FCSTD DOCUMENT  (FreeCAD 0.18R16146 (Git))
Label: body_polywood_8mm
License: All rights reserved
LicenseURL: http://en.wikipedia.org/wiki/All_rights_reserved
objects: Sketcher::SketchObject×6
note: 6 computed .brp shape members not serialized (recipe doc carries the construction recipe); baked Part::Feature solids carry a one-line shape summary decoded from their .brp

FEATURE [Sketcher::SketchObject] Sketch  label="bottom"
  sketch-geometry (118):
    g0: LineSegment [constr] StartX=-110 StartY=110 StartZ=0 EndX=110 EndY=110 EndZ=0
    g1: LineSegment [constr] StartX=110 StartY=110 StartZ=0 EndX=110 EndY=-110 EndZ=0
    g2: LineSegment [constr] StartX=110 StartY=-110 StartZ=0 EndX=-110 EndY=-110 EndZ=0
    g3: LineSegment [constr] StartX=-110 StartY=-110 StartZ=0 EndX=-110 EndY=110 EndZ=0
    g4: Circle CenterX=-104.5 CenterY=104.5 CenterZ=0 NormalX=0 NormalY=0 NormalZ=1 AngleXU=0 Radius=1.55
    g5: Circle CenterX=104.5 CenterY=104.5 CenterZ=0 NormalX=0 NormalY=0 NormalZ=1 AngleXU=0 Radius=1.55
    g6: Circle CenterX=-104.5 CenterY=-104.5 CenterZ=0 NormalX=0 NormalY=0 NormalZ=1 AngleXU=0 Radius=1.55
    g7: Circle CenterX=104.5 CenterY=-104.5 CenterZ=0 NormalX=0 NormalY=0 NormalZ=1 AngleXU=0 Radius=1.55
    g8: LineSegment [constr] StartX=-104.5 StartY=104.5 StartZ=0 EndX=104.5 EndY=104.5 EndZ=0
    g9: LineSegment [constr] StartX=104.5 StartY=104.5 StartZ=0 EndX=104.5 EndY=-104.5 EndZ=0
    g10: LineSegment [constr] StartX=104.5 StartY=-104.5 StartZ=0 EndX=-104.5 EndY=-104.5 EndZ=0
    g11: LineSegment [constr] StartX=-104.5 StartY=-104.5 StartZ=0 EndX=-104.5 EndY=104.5 EndZ=0
    g12: LineSegment [constr] StartX=0 StartY=0 StartZ=0 EndX=0 EndY=210 EndZ=0
    g13: LineSegment [constr] StartX=0 StartY=0 StartZ=0 EndX=181.865 EndY=-105 EndZ=0
    g14: LineSegment [constr] StartX=0 StartY=0 StartZ=0 EndX=-181.865 EndY=-105 EndZ=0
    g15: LineSegment [constr] StartX=-33 StartY=202.5 StartZ=0 EndX=33 EndY=202.5 EndZ=0
    g16: Circle CenterX=-33 CenterY=202.5 CenterZ=0 NormalX=0 NormalY=0 NormalZ=1 AngleXU=0 Radius=2.1
    g17: Circle CenterX=33 CenterY=202.5 CenterZ=0 NormalX=0 NormalY=0 NormalZ=1 AngleXU=0 Radius=2.1
    g18: LineSegment [constr] StartX=158.87 StartY=-129.829 StartZ=0 EndX=191.87 EndY=-72.6712 EndZ=0
    g19: LineSegment [constr] StartX=-158.87 StartY=-129.829 StartZ=0 EndX=-191.87 EndY=-72.6712 EndZ=0
    g20: GeomPoint X=-175.37 Y=-101.25 Z=0
    g21: GeomPoint X=175.37 Y=-101.25 Z=0
    g22: Circle CenterX=-158.87 CenterY=-129.829 CenterZ=0 NormalX=0 NormalY=0 NormalZ=1 AngleXU=0 Radius=2.1
    g23: Circle CenterX=-191.87 CenterY=-72.6712 CenterZ=0 NormalX=0 NormalY=0 NormalZ=1 AngleXU=0 Radius=2.1
    g24: Circle CenterX=158.87 CenterY=-129.829 CenterZ=0 NormalX=0 NormalY=0 NormalZ=1 AngleXU=0 Radius=2.1
    g25: Circle CenterX=191.87 CenterY=-72.6712 CenterZ=0 NormalX=0 NormalY=0 NormalZ=1 AngleXU=0 Radius=2.1
    g26: LineSegment [constr] StartX=-202.5 StartY=-139.829 StartZ=0 EndX=202.5 EndY=-139.829 EndZ=0
    g27: LineSegment [constr] StartX=202.5 StartY=-139.829 StartZ=0 EndX=202.5 EndY=210 EndZ=0
    g28: LineSegment [constr] StartX=202.5 StartY=210 StartZ=0 EndX=-202.5 EndY=210 EndZ=0
    g29: LineSegment [constr] StartX=-202.5 StartY=210 StartZ=0 EndX=-202.5 EndY=-139.829 EndZ=0
    g30: LineSegment [constr] StartX=-145.5 StartY=-139.829 StartZ=0 EndX=-115.5 EndY=-139.829 EndZ=0
    g31: LineSegment StartX=-115.5 StartY=-139.829 StartZ=0 EndX=-115.5 EndY=-147.829 EndZ=0
    g32: LineSegment StartX=-115.5 StartY=-147.829 StartZ=0 EndX=-145.5 EndY=-147.829 EndZ=0
    g33: LineSegment StartX=-145.5 StartY=-147.829 StartZ=0 EndX=-145.5 EndY=-139.829 EndZ=0
    g34: LineSegment [constr] StartX=-58.5 StartY=-139.829 StartZ=0 EndX=-28.5 EndY=-139.829 EndZ=0
    g35: LineSegment StartX=-28.5 StartY=-139.829 StartZ=0 EndX=-28.5 EndY=-147.829 EndZ=0
    g36: LineSegment StartX=-28.5 StartY=-147.829 StartZ=0 EndX=-58.5 EndY=-147.829 EndZ=0
    g37: LineSegment StartX=-58.5 StartY=-147.829 StartZ=0 EndX=-58.5 EndY=-139.829 EndZ=0
    g38: LineSegment [constr] StartX=28.5 StartY=-139.829 StartZ=0 EndX=58.5 EndY=-139.829 EndZ=0
    g39: LineSegment StartX=58.5 StartY=-139.829 StartZ=0 EndX=58.5 EndY=-147.829 EndZ=0
    g40: LineSegment StartX=58.5 StartY=-147.829 StartZ=0 EndX=28.5 EndY=-147.829 EndZ=0
    g41: LineSegment StartX=28.5 StartY=-147.829 StartZ=0 EndX=28.5 EndY=-139.829 EndZ=0
    g42: LineSegment [constr] StartX=115.5 StartY=-139.829 StartZ=0 EndX=145.5 EndY=-139.829 EndZ=0
    g43: LineSegment StartX=145.5 StartY=-139.829 StartZ=0 EndX=145.5 EndY=-147.829 EndZ=0
    g44: LineSegment StartX=145.5 StartY=-147.829 StartZ=0 EndX=115.5 EndY=-147.829 EndZ=0
    g45: LineSegment StartX=115.5 StartY=-147.829 StartZ=0 EndX=115.5 EndY=-139.829 EndZ=0
    g46: LineSegment StartX=202.5 StartY=-63.8631 StartZ=0 EndX=210.5 EndY=-63.8631 EndZ=0
    g47: LineSegment StartX=210.5 StartY=-63.8631 StartZ=0 EndX=210.5 EndY=-93.8631 EndZ=0
    g48: LineSegment StartX=210.5 StartY=-93.8631 StartZ=0 EndX=202.5 EndY=-93.8631 EndZ=0
    g49: LineSegment [constr] StartX=202.5 StartY=-93.8631 StartZ=0 EndX=202.5 EndY=-63.8631 EndZ=0
    g50: LineSegment StartX=202.5 StartY=12.1027 StartZ=0 EndX=210.5 EndY=12.1027 EndZ=0
    g51: LineSegment StartX=210.5 StartY=12.1027 StartZ=0 EndX=210.5 EndY=-17.8973 EndZ=0
    g52: LineSegment StartX=210.5 StartY=-17.8973 StartZ=0 EndX=202.5 EndY=-17.8973 EndZ=0
    g53: LineSegment [constr] StartX=202.5 StartY=-17.8973 StartZ=0 EndX=202.5 EndY=12.1027 EndZ=0
    g54: LineSegment StartX=202.5 StartY=88.0685 StartZ=0 EndX=210.5 EndY=88.0685 EndZ=0
    g55: LineSegment StartX=210.5 StartY=88.0685 StartZ=0 EndX=210.5 EndY=58.0685 EndZ=0
    g56: LineSegment StartX=210.5 StartY=58.0685 StartZ=0 EndX=202.5 EndY=58.0685 EndZ=0
    g57: LineSegment [constr] StartX=202.5 StartY=58.0685 StartZ=0 EndX=202.5 EndY=88.0685 EndZ=0
    g58: LineSegment StartX=202.5 StartY=164.034 StartZ=0 EndX=210.5 EndY=164.034 EndZ=0
    g59: LineSegment StartX=210.5 StartY=164.034 StartZ=0 EndX=210.5 EndY=134.034 EndZ=0
    g60: LineSegment StartX=210.5 StartY=134.034 StartZ=0 EndX=202.5 EndY=134.034 EndZ=0
    g61: LineSegment [constr] StartX=202.5 StartY=134.034 StartZ=0 EndX=202.5 EndY=164.034 EndZ=0
    g62: LineSegment StartX=-145.5 StartY=218 StartZ=0 EndX=-115.5 EndY=218 EndZ=0
    g63: LineSegment StartX=-115.5 StartY=218 StartZ=0 EndX=-115.5 EndY=210 EndZ=0
    g64: LineSegment [constr] StartX=-115.5 StartY=210 StartZ=0 EndX=-145.5 EndY=210 EndZ=0
    g65: LineSegment StartX=-145.5 StartY=210 StartZ=0 EndX=-145.5 EndY=218 EndZ=0
    g66: LineSegment StartX=-58.5 StartY=218 StartZ=0 EndX=-28.5 EndY=218 EndZ=0
    g67: LineSegment StartX=-28.5 StartY=218 StartZ=0 EndX=-28.5 EndY=210 EndZ=0
    g68: LineSegment [constr] StartX=-28.5 StartY=210 StartZ=0 EndX=-58.5 EndY=210 EndZ=0
    g69: LineSegment StartX=-58.5 StartY=210 StartZ=0 EndX=-58.5 EndY=218 EndZ=0
    g70: LineSegment StartX=28.5 StartY=218 StartZ=0 EndX=58.5 EndY=218 EndZ=0
    g71: LineSegment StartX=58.5 StartY=218 StartZ=0 EndX=58.5 EndY=210 EndZ=0
    g72: LineSegment [constr] StartX=58.5 StartY=210 StartZ=0 EndX=28.5 EndY=210 EndZ=0
    g73: LineSegment StartX=28.5 StartY=210 StartZ=0 EndX=28.5 EndY=218 EndZ=0
    g74: LineSegment StartX=115.5 StartY=218 StartZ=0 EndX=145.5 EndY=218 EndZ=0
    g75: LineSegment StartX=145.5 StartY=218 StartZ=0 EndX=145.5 EndY=210 EndZ=0
    g76: LineSegment [constr] StartX=145.5 StartY=210 StartZ=0 EndX=115.5 EndY=210 EndZ=0
    g77: LineSegment StartX=115.5 StartY=210 StartZ=0 EndX=115.5 EndY=218 EndZ=0
    g78: LineSegment StartX=-210.5 StartY=164.034 StartZ=0 EndX=-202.5 EndY=164.034 EndZ=0
    g79: LineSegment [constr] StartX=-202.5 StartY=164.034 StartZ=0 EndX=-202.5 EndY=134.034 EndZ=0
    g80: LineSegment StartX=-202.5 StartY=134.034 StartZ=0 EndX=-210.5 EndY=134.034 EndZ=0
    g81: LineSegment StartX=-210.5 StartY=134.034 StartZ=0 EndX=-210.5 EndY=164.034 EndZ=0
    g82: LineSegment StartX=-210.5 StartY=88.0685 StartZ=0 EndX=-202.5 EndY=88.0685 EndZ=0
    g83: LineSegment [constr] StartX=-202.5 StartY=88.0685 StartZ=0 EndX=-202.5 EndY=58.0685 EndZ=0
    g84: LineSegment StartX=-202.5 StartY=58.0685 StartZ=0 EndX=-210.5 EndY=58.0685 EndZ=0
    g85: LineSegment StartX=-210.5 StartY=58.0685 StartZ=0 EndX=-210.5 EndY=88.0685 EndZ=0
    g86: LineSegment StartX=-210.5 StartY=12.1027 StartZ=0 EndX=-202.5 EndY=12.1027 EndZ=0
    g87: LineSegment [constr] StartX=-202.5 StartY=12.1027 StartZ=0 EndX=-202.5 EndY=-17.8973 EndZ=0
    g88: LineSegment StartX=-202.5 StartY=-17.8973 StartZ=0 EndX=-210.5 EndY=-17.8973 EndZ=0
    g89: LineSegment StartX=-210.5 StartY=-17.8973 StartZ=0 EndX=-210.5 EndY=12.1027 EndZ=0
    g90: LineSegment StartX=-210.5 StartY=-63.8631 StartZ=0 EndX=-202.5 EndY=-63.8631 EndZ=0
    g91: LineSegment [constr] StartX=-202.5 StartY=-63.8631 StartZ=0 EndX=-202.5 EndY=-93.8631 EndZ=0
    g92: LineSegment StartX=-202.5 StartY=-93.8631 StartZ=0 EndX=-210.5 EndY=-93.8631 EndZ=0
    g93: LineSegment StartX=-210.5 StartY=-93.8631 StartZ=0 EndX=-210.5 EndY=-63.8631 EndZ=0
    g94: LineSegment StartX=-28.5 StartY=-139.829 StartZ=0 EndX=28.5 EndY=-139.829 EndZ=0
    g95: LineSegment StartX=58.5 StartY=-139.829 StartZ=0 EndX=115.5 EndY=-139.829 EndZ=0
    g96: LineSegment StartX=145.5 StartY=-139.829 StartZ=0 EndX=202.5 EndY=-139.829 EndZ=0
    g97: LineSegment StartX=202.5 StartY=-139.829 StartZ=0 EndX=202.5 EndY=-93.8631 EndZ=0
    g98: LineSegment StartX=202.5 StartY=-63.8631 StartZ=0 EndX=202.5 EndY=-17.8973 EndZ=0
    g99: LineSegment StartX=202.5 StartY=12.1027 StartZ=0 EndX=202.5 EndY=58.0685 EndZ=0
    g100: LineSegment StartX=202.5 StartY=88.0685 StartZ=0 EndX=202.5 EndY=134.034 EndZ=0
    g101: LineSegment StartX=202.5 StartY=164.034 StartZ=0 EndX=202.5 EndY=210 EndZ=0
    g102: LineSegment StartX=145.5 StartY=210 StartZ=0 EndX=202.5 EndY=210 EndZ=0
    g103: LineSegment StartX=58.5 StartY=210 StartZ=0 EndX=115.5 EndY=210 EndZ=0
    g104: LineSegment StartX=-28.5 StartY=210 StartZ=0 EndX=28.5 EndY=210 EndZ=0
    g105: LineSegment StartX=-115.5 StartY=210 StartZ=0 EndX=-58.5 EndY=210 EndZ=0
    g106: LineSegment StartX=-202.5 StartY=210 StartZ=0 EndX=-145.5 EndY=210 EndZ=0
    g107: LineSegment StartX=-202.5 StartY=164.034 StartZ=0 EndX=-202.5 EndY=210 EndZ=0
    g108: LineSegment StartX=-202.5 StartY=88.0685 StartZ=0 EndX=-202.5 EndY=134.034 EndZ=0
    g109: LineSegment StartX=-202.5 StartY=12.1027 StartZ=0 EndX=-202.5 EndY=58.0685 EndZ=0
    g110: LineSegment StartX=-202.5 StartY=-63.8631 StartZ=0 EndX=-202.5 EndY=-17.8973 EndZ=0
    g111: LineSegment StartX=-202.5 StartY=-139.829 StartZ=0 EndX=-202.5 EndY=-93.8631 EndZ=0
    g112: LineSegment StartX=-202.5 StartY=-139.829 StartZ=0 EndX=-145.5 EndY=-139.829 EndZ=0
    g113: LineSegment StartX=-115.5 StartY=-139.829 StartZ=0 EndX=-58.5 EndY=-139.829 EndZ=0
    g114: Circle CenterX=-193.5 CenterY=201 CenterZ=0 NormalX=0 NormalY=0 NormalZ=1 AngleXU=0 Radius=1.55
    g115: Circle CenterX=193.5 CenterY=201 CenterZ=0 NormalX=0 NormalY=0 NormalZ=1 AngleXU=0 Radius=1.55
    g116: Circle CenterX=193.5 CenterY=-130.829 CenterZ=0 NormalX=0 NormalY=0 NormalZ=1 AngleXU=0 Radius=1.55
    g117: Circle CenterX=-193.5 CenterY=-130.829 CenterZ=0 NormalX=0 NormalY=0 NormalZ=1 AngleXU=0 Radius=1.55
  constraints (319):
    c: Coincident(g0,g1)
    c: Coincident(g1,g2)
    c: Coincident(g2,g3)
    c: Coincident(g3,g0)
    c: Horizontal(g0)
    c: Vertical(g3)
    c: Symmetric(g2,g1,g-2)
    c: Symmetric(g0,g1,g-1)
    c: DistanceX(g0,g0) = 220
    c: DistanceY(g1,g1) = 220
    c: Coincident(g8,g9)
    c: Coincident(g9,g10)
    c: Coincident(g10,g11)
    c: Coincident(g11,g8)
    c: Horizontal(g8)
    c: Horizontal(g10)
    c: Vertical(g9)
    c: Vertical(g11)
    c: Coincident(g7,g9)
    c: Coincident(g6,g10)
    c: Coincident(g4,g8)
    c: Coincident(g5,g8)
    c: DistanceY(g4,g0) = 5.5
    c: DistanceX(g0,g4) = 5.5
    c: DistanceX(g5,g0) = 5.5
    c: DistanceY(g2,g6) = 5.5
    c: Radius(g6) = 1.55
    c: Equal(g6,g7)
    c: Equal(g6,g4)
    c: Equal(g6,g5)
    c: Coincident(g12,g13)
    c: Coincident(g12,g14)
    c: Coincident(g12,g-1)
    c: Vertical(g12)
    c: Angle(g13,g12) = 2.0944
    c: Angle(g12,g14) = 2.0944
    c: Equal(g14,g12)
    c: Equal(g12,g13)
    c: DistanceY(g12,g12) = 210
    c: DistanceX(g15,g15) = 66
    c: Symmetric(g15,g15,g12)
    c: DistanceY(g15,g12) = 7.5
    c: Coincident(g15,g17)
    c: Coincident(g15,g16)
    c: Radius(g16) = 2.1
    c: Equal(g16,g17)
    c: Symmetric(g19,g19,g14)
    c: Symmetric(g18,g18,g13)
    c: Distance(g18) = 66
    c: Distance(g19) = 66
    c: PointOnObject(g20,g14)
    c: PointOnObject(g20,g19)
    c: Distance(g14,g20) = 7.5
    c: PointOnObject(g21,g13)
    c: PointOnObject(g21,g18)
    c: Distance(g21,g13) = 7.5
    c: Coincident(g18,g25)
    c: Coincident(g18,g24)
    c: Coincident(g19,g22)
    c: Coincident(g19,g23)
    c: Equal(g23,g22)
    c: Equal(g22,g24)
    c: Equal(g24,g25)
    c: Equal(g25,g17)
    c: Coincident(g26,g27)
    c: Coincident(g27,g28)
    c: Coincident(g28,g29)
    c: Coincident(g29,g26)
    c: Horizontal(g28)
    c: Vertical(g27)
    c: Vertical(g29)
    c: DistanceY(g16,g28) = 7.5
    c: DistanceY(g26,g24) = 10
    c: Coincident(g30,g31)
    c: Coincident(g31,g32)
    c: Coincident(g32,g33)
    c: Coincident(g33,g30)
    c: Horizontal(g30)
    c: Horizontal(g32)
    c: Vertical(g31)
    c: Vertical(g33)
    c: Coincident(g34,g35)
    c: Coincident(g35,g36)
    c: Coincident(g36,g37)
    c: Coincident(g37,g34)
    c: Horizontal(g34)
    c: Horizontal(g36)
    c: Vertical(g35)
    c: Vertical(g37)
    c: Coincident(g38,g39)
    c: Coincident(g39,g40)
    c: Coincident(g40,g41)
    c: Coincident(g41,g38)
    c: Horizontal(g38)
    c: Horizontal(g40)
    c: Vertical(g39)
    c: Vertical(g41)
    c: Coincident(g42,g43)
    c: Coincident(g43,g44)
    c: Coincident(g44,g45)
    c: Coincident(g45,g42)
    c: Horizontal(g42)
    c: Horizontal(g44)
    c: Vertical(g43)
    c: Vertical(g45)
    c: Coincident(g46,g47)
    c: Coincident(g47,g48)
    c: Coincident(g48,g49)
    c: Coincident(g49,g46)
    c: Horizontal(g46)
    c: Horizontal(g48)
    c: Vertical(g47)
    c: Vertical(g49)
    c: Coincident(g50,g51)
    c: Coincident(g51,g52)
    c: Coincident(g52,g53)
    c: Coincident(g53,g50)
    c: Horizontal(g50)
    c: Horizontal(g52)
    c: Vertical(g51)
    c: Vertical(g53)
    c: Coincident(g54,g55)
    c: Coincident(g55,g56)
    c: Coincident(g56,g57)
    c: Coincident(g57,g54)
    c: Horizontal(g54)
    c: Horizontal(g56)
    c: Vertical(g55)
    c: Vertical(g57)
    c: Coincident(g58,g59)
    c: Coincident(g59,g60)
    c: Coincident(g60,g61)
    c: Coincident(g61,g58)
    c: Horizontal(g58)
    c: Horizontal(g60)
    c: Vertical(g59)
    c: Vertical(g61)
    c: Coincident(g62,g63)
    c: Coincident(g63,g64)
    c: Coincident(g64,g65)
    c: Coincident(g65,g62)
    c: Horizontal(g62)
    c: Horizontal(g64)
    c: Vertical(g63)
    c: Vertical(g65)
    c: Coincident(g66,g67)
    c: Coincident(g67,g68)
    c: Coincident(g68,g69)
    c: Coincident(g69,g66)
    c: Horizontal(g66)
    c: Horizontal(g68)
    c: Vertical(g67)
    c: Vertical(g69)
    c: Coincident(g70,g71)
    c: Coincident(g71,g72)
    c: Coincident(g72,g73)
    c: Coincident(g73,g70)
    c: Horizontal(g70)
    c: Horizontal(g72)
    c: Vertical(g71)
    c: Vertical(g73)
    c: Coincident(g74,g75)
    c: Coincident(g75,g76)
    c: Coincident(g76,g77)
    c: Coincident(g77,g74)
    c: Horizontal(g74)
    c: Horizontal(g76)
    c: Vertical(g75)
    c: Vertical(g77)
    c: Coincident(g78,g79)
    c: Coincident(g79,g80)
    c: Coincident(g80,g81)
    c: Coincident(g81,g78)
    c: Horizontal(g78)
    c: Horizontal(g80)
    c: Vertical(g79)
    c: Vertical(g81)
    c: Coincident(g82,g83)
    c: Coincident(g83,g84)
    c: Coincident(g84,g85)
    c: Coincident(g85,g82)
    c: Horizontal(g82)
    c: Horizontal(g84)
    c: Vertical(g83)
    c: Vertical(g85)
    c: Coincident(g86,g87)
    c: Coincident(g87,g88)
    c: Coincident(g88,g89)
    c: Coincident(g89,g86)
    c: Horizontal(g86)
    c: Horizontal(g88)
    c: Vertical(g87)
    c: Vertical(g89)
    c: Coincident(g90,g91)
    c: Coincident(g91,g92)
    c: Coincident(g92,g93)
    c: Coincident(g93,g90)
    c: Horizontal(g90)
    c: Horizontal(g92)
    c: Vertical(g91)
    c: Vertical(g93)
    c: PointOnObject(g34,g26)
    c: PointOnObject(g30,g26)
    c: PointOnObject(g91,g29)
    c: PointOnObject(g87,g29)
    c: PointOnObject(g83,g29)
    c: PointOnObject(g79,g29)
    c: PointOnObject(g64,g28)
    c: PointOnObject(g68,g28)
    c: PointOnObject(g72,g28)
    c: PointOnObject(g76,g28)
    c: PointOnObject(g60,g27)
    c: PointOnObject(g56,g27)
    c: PointOnObject(g52,g27)
    c: PointOnObject(g48,g27)
    c: PointOnObject(g42,g26)
    c: PointOnObject(g38,g26)
    c: Equal(g39,g45)
    c: Equal(g45,g48)
    c: Equal(g48,g52)
    c: Equal(g52,g56)
    c: Equal(g56,g60)
    c: Equal(g60,g75)
    c: Equal(g75,g71)
    c: Equal(g71,g67)
    c: Equal(g67,g63)
    c: Equal(g63,g78)
    c: Equal(g78,g82)
    c: Equal(g82,g86)
    c: Equal(g86,g90)
    c: Equal(g90,g33)
    c: Equal(g33,g37)
    c: DistanceY(g65,g65) = 8
    c: Equal(g32,g36)
    c: Equal(g36,g40)
    c: Equal(g40,g44)
    c: Equal(g44,g47)
    c: Equal(g47,g51)
    c: Equal(g51,g55)
    c: Equal(g55,g59)
    c: Equal(g59,g74)
    c: Equal(g74,g70)
    c: Equal(g70,g66)
    c: Equal(g66,g62)
    c: Equal(g62,g81)
    c: Equal(g81,g85)
    c: Equal(g85,g89)
    c: Equal(g89,g93)
    c: DistanceX(g62,g62) = 30
    c: Coincident(g113,g30)
    c: Coincident(g113,g34)
    c: Coincident(g34,g94)
    c: Coincident(g38,g94)
    c: Coincident(g38,g95)
    c: Coincident(g42,g95)
    c: Coincident(g96,g42)
    c: Coincident(g26,g96)
    c: Coincident(g26,g97)
    c: Coincident(g48,g97)
    c: Coincident(g46,g98)
    c: Coincident(g52,g98)
    c: Coincident(g50,g99)
    c: Coincident(g56,g99)
    c: Coincident(g54,g100)
    c: Coincident(g60,g100)
    c: Coincident(g58,g101)
    c: Coincident(g27,g101)
    c: Coincident(g27,g102)
    c: Coincident(g75,g102)
    c: Coincident(g76,g103)
    c: Coincident(g71,g103)
    c: Coincident(g72,g104)
    c: Coincident(g67,g104)
    c: Coincident(g68,g105)
    c: Coincident(g63,g105)
    c: Coincident(g64,g106)
    c: Coincident(g28,g106)
    c: Coincident(g28,g107)
    c: Coincident(g78,g107)
    c: Coincident(g82,g108)
    c: Coincident(g79,g108)
    c: Coincident(g86,g109)
    c: Coincident(g83,g109)
    c: Coincident(g90,g110)
    c: Coincident(g87,g110)
    c: Coincident(g91,g111)
    c: Coincident(g26,g111)
    c: Coincident(g26,g112)
    c: Coincident(g30,g112)
    c: Equal(g97,g98)
    c: Equal(g98,g99)
    c: Equal(g99,g100)
    c: Equal(g100,g101)
    c: Equal(g106,g105)
    c: Equal(g105,g104)
    c: Equal(g104,g103)
    c: Equal(g103,g102)
    c: Equal(g107,g108)
    c: Equal(g108,g109)
    c: Equal(g109,g110)
    c: Equal(g110,g111)
    c: Equal(g112,g113)
    c: Equal(g113,g94)
    c: Equal(g94,g95)
    c: Equal(g95,g96)
    c: Symmetric(g111,g96,g-2)
    c: DistanceX(g111,g96) = 405
    c: DistanceX(g106,g114) = 9
    c: DistanceY(g114,g106) = 9
    c: Radius(g114) = 1.55
    c: DistanceX(g115,g101) = 9
    c: DistanceY(g115,g101) = 9
    c: Radius(g115) = 1.55
    c: DistanceX(g116,g96) = 9
    c: DistanceY(g96,g116) = 9
    c: Radius(g116) = 1.55
    c: DistanceX(g111,g117) = 9
    c: DistanceY(g111,g117) = 9
    c: Radius(g117) = 1.55
FEATURE [Sketcher::SketchObject] Sketch001  label="top"
  sketch-geometry (153):
    g0: LineSegment [constr] StartX=-110 StartY=110 StartZ=0 EndX=110 EndY=110 EndZ=0
    g1: LineSegment [constr] StartX=110 StartY=110 StartZ=0 EndX=110 EndY=-110 EndZ=0
    g2: LineSegment [constr] StartX=110 StartY=-110 StartZ=0 EndX=-110 EndY=-110 EndZ=0
    g3: LineSegment [constr] StartX=-110 StartY=-110 StartZ=0 EndX=-110 EndY=110 EndZ=0
    g4: Circle [constr] CenterX=-104.5 CenterY=104.5 CenterZ=0 NormalX=0 NormalY=0 NormalZ=1 AngleXU=0 Radius=1.55
    g5: Circle [constr] CenterX=104.5 CenterY=104.5 CenterZ=0 NormalX=0 NormalY=0 NormalZ=1 AngleXU=0 Radius=1.55
    g6: Circle [constr] CenterX=-104.5 CenterY=-104.5 CenterZ=0 NormalX=0 NormalY=0 NormalZ=1 AngleXU=0 Radius=1.55
    g7: Circle [constr] CenterX=104.5 CenterY=-104.5 CenterZ=0 NormalX=0 NormalY=0 NormalZ=1 AngleXU=0 Radius=1.55
    g8: LineSegment [constr] StartX=-104.5 StartY=104.5 StartZ=0 EndX=104.5 EndY=104.5 EndZ=0
    g9: LineSegment [constr] StartX=104.5 StartY=104.5 StartZ=0 EndX=104.5 EndY=-104.5 EndZ=0
    g10: LineSegment [constr] StartX=104.5 StartY=-104.5 StartZ=0 EndX=-104.5 EndY=-104.5 EndZ=0
    g11: LineSegment [constr] StartX=-104.5 StartY=-104.5 StartZ=0 EndX=-104.5 EndY=104.5 EndZ=0
    g12: LineSegment [constr] StartX=0 StartY=0 StartZ=0 EndX=0 EndY=210 EndZ=0
    g13: LineSegment [constr] StartX=0 StartY=0 StartZ=0 EndX=181.865 EndY=-105 EndZ=0
    g14: LineSegment [constr] StartX=0 StartY=0 StartZ=0 EndX=-181.865 EndY=-105 EndZ=0
    g15: LineSegment [constr] StartX=-33 StartY=202.5 StartZ=0 EndX=33 EndY=202.5 EndZ=0
    g16: Circle CenterX=-33 CenterY=202.5 CenterZ=0 NormalX=0 NormalY=0 NormalZ=1 AngleXU=0 Radius=2.1
    g17: Circle CenterX=33 CenterY=202.5 CenterZ=0 NormalX=0 NormalY=0 NormalZ=1 AngleXU=0 Radius=2.1
    g18: LineSegment [constr] StartX=158.87 StartY=-129.829 StartZ=0 EndX=191.87 EndY=-72.6712 EndZ=0
    g19: LineSegment [constr] StartX=-158.87 StartY=-129.829 StartZ=0 EndX=-191.87 EndY=-72.6712 EndZ=0
    g20: GeomPoint X=-175.37 Y=-101.25 Z=0
    g21: GeomPoint X=175.37 Y=-101.25 Z=0
    g22: Circle CenterX=-158.87 CenterY=-129.829 CenterZ=0 NormalX=0 NormalY=0 NormalZ=1 AngleXU=0 Radius=2.1
    g23: Circle CenterX=-191.87 CenterY=-72.6712 CenterZ=0 NormalX=0 NormalY=0 NormalZ=1 AngleXU=0 Radius=2.1
    g24: Circle CenterX=158.87 CenterY=-129.829 CenterZ=0 NormalX=0 NormalY=0 NormalZ=1 AngleXU=0 Radius=2.1
    g25: Circle CenterX=191.87 CenterY=-72.6712 CenterZ=0 NormalX=0 NormalY=0 NormalZ=1 AngleXU=0 Radius=2.1
    g26: LineSegment [constr] StartX=-202.5 StartY=-140 StartZ=0 EndX=202.5 EndY=-140 EndZ=0
    g27: LineSegment [constr] StartX=202.5 StartY=-140 StartZ=0 EndX=202.5 EndY=210 EndZ=0
    g28: LineSegment [constr] StartX=202.5 StartY=210 StartZ=0 EndX=-202.5 EndY=210 EndZ=0
    g29: LineSegment [constr] StartX=-202.5 StartY=210 StartZ=0 EndX=-202.5 EndY=-140 EndZ=0
    g30: LineSegment [constr] StartX=-145.5 StartY=-140 StartZ=0 EndX=-115.5 EndY=-140 EndZ=0
    g31: LineSegment StartX=-115.5 StartY=-140 StartZ=0 EndX=-115.5 EndY=-148 EndZ=0
    g32: LineSegment StartX=-115.5 StartY=-148 StartZ=0 EndX=-145.5 EndY=-148 EndZ=0
    g33: LineSegment StartX=-145.5 StartY=-148 StartZ=0 EndX=-145.5 EndY=-140 EndZ=0
    g34: LineSegment [constr] StartX=-58.5 StartY=-140 StartZ=0 EndX=-28.5 EndY=-140 EndZ=0
    g35: LineSegment StartX=-28.5 StartY=-140 StartZ=0 EndX=-28.5 EndY=-148 EndZ=0
    g36: LineSegment StartX=-28.5 StartY=-148 StartZ=0 EndX=-58.5 EndY=-148 EndZ=0
    g37: LineSegment StartX=-58.5 StartY=-148 StartZ=0 EndX=-58.5 EndY=-140 EndZ=0
    g38: LineSegment [constr] StartX=28.5 StartY=-140 StartZ=0 EndX=58.5 EndY=-140 EndZ=0
    g39: LineSegment StartX=58.5 StartY=-140 StartZ=0 EndX=58.5 EndY=-148 EndZ=0
    g40: LineSegment StartX=58.5 StartY=-148 StartZ=0 EndX=28.5 EndY=-148 EndZ=0
    g41: LineSegment StartX=28.5 StartY=-148 StartZ=0 EndX=28.5 EndY=-140 EndZ=0
    g42: LineSegment [constr] StartX=115.5 StartY=-140 StartZ=0 EndX=145.5 EndY=-140 EndZ=0
    g43: LineSegment StartX=145.5 StartY=-140 StartZ=0 EndX=145.5 EndY=-148 EndZ=0
    g44: LineSegment StartX=145.5 StartY=-148 StartZ=0 EndX=115.5 EndY=-148 EndZ=0
    g45: LineSegment StartX=115.5 StartY=-148 StartZ=0 EndX=115.5 EndY=-140 EndZ=0
    g46: LineSegment StartX=202.5 StartY=-64 StartZ=0 EndX=210.5 EndY=-64 EndZ=0
    g47: LineSegment StartX=210.5 StartY=-64 StartZ=0 EndX=210.5 EndY=-94 EndZ=0
    g48: LineSegment StartX=210.5 StartY=-94 StartZ=0 EndX=202.5 EndY=-94 EndZ=0
    g49: LineSegment [constr] StartX=202.5 StartY=-94 StartZ=0 EndX=202.5 EndY=-64 EndZ=0
    g50: LineSegment StartX=202.5 StartY=12 StartZ=0 EndX=210.5 EndY=12 EndZ=0
    g51: LineSegment StartX=210.5 StartY=12 StartZ=0 EndX=210.5 EndY=-18 EndZ=0
    g52: LineSegment StartX=210.5 StartY=-18 StartZ=0 EndX=202.5 EndY=-18 EndZ=0
    g53: LineSegment [constr] StartX=202.5 StartY=-18 StartZ=0 EndX=202.5 EndY=12 EndZ=0
    g54: LineSegment StartX=202.5 StartY=88 StartZ=0 EndX=210.5 EndY=88 EndZ=0
    g55: LineSegment StartX=210.5 StartY=88 StartZ=0 EndX=210.5 EndY=58 EndZ=0
    g56: LineSegment StartX=210.5 StartY=58 StartZ=0 EndX=202.5 EndY=58 EndZ=0
    g57: LineSegment [constr] StartX=202.5 StartY=58 StartZ=0 EndX=202.5 EndY=88 EndZ=0
    g58: LineSegment StartX=202.5 StartY=164 StartZ=0 EndX=210.5 EndY=164 EndZ=0
    g59: LineSegment StartX=210.5 StartY=164 StartZ=0 EndX=210.5 EndY=134 EndZ=0
    g60: LineSegment StartX=210.5 StartY=134 StartZ=0 EndX=202.5 EndY=134 EndZ=0
    g61: LineSegment [constr] StartX=202.5 StartY=134 StartZ=0 EndX=202.5 EndY=164 EndZ=0
    g62: LineSegment StartX=-145.5 StartY=218 StartZ=0 EndX=-115.5 EndY=218 EndZ=0
    g63: LineSegment StartX=-115.5 StartY=218 StartZ=0 EndX=-115.5 EndY=210 EndZ=0
    g64: LineSegment [constr] StartX=-115.5 StartY=210 StartZ=0 EndX=-145.5 EndY=210 EndZ=0
    g65: LineSegment StartX=-145.5 StartY=210 StartZ=0 EndX=-145.5 EndY=218 EndZ=0
    g66: LineSegment StartX=-58.5 StartY=218 StartZ=0 EndX=-28.5 EndY=218 EndZ=0
    g67: LineSegment StartX=-28.5 StartY=218 StartZ=0 EndX=-28.5 EndY=210 EndZ=0
    g68: LineSegment [constr] StartX=-28.5 StartY=210 StartZ=0 EndX=-58.5 EndY=210 EndZ=0
    g69: LineSegment StartX=-58.5 StartY=210 StartZ=0 EndX=-58.5 EndY=218 EndZ=0
    g70: LineSegment StartX=28.5 StartY=218 StartZ=0 EndX=58.5 EndY=218 EndZ=0
    g71: LineSegment StartX=58.5 StartY=218 StartZ=0 EndX=58.5 EndY=210 EndZ=0
    g72: LineSegment [constr] StartX=58.5 StartY=210 StartZ=0 EndX=28.5 EndY=210 EndZ=0
    g73: LineSegment StartX=28.5 StartY=210 StartZ=0 EndX=28.5 EndY=218 EndZ=0
    g74: LineSegment StartX=115.5 StartY=218 StartZ=0 EndX=145.5 EndY=218 EndZ=0
    g75: LineSegment StartX=145.5 StartY=218 StartZ=0 EndX=145.5 EndY=210 EndZ=0
    g76: LineSegment [constr] StartX=145.5 StartY=210 StartZ=0 EndX=115.5 EndY=210 EndZ=0
    g77: LineSegment StartX=115.5 StartY=210 StartZ=0 EndX=115.5 EndY=218 EndZ=0
    g78: LineSegment StartX=-210.5 StartY=164 StartZ=0 EndX=-202.5 EndY=164 EndZ=0
    g79: LineSegment [constr] StartX=-202.5 StartY=164 StartZ=0 EndX=-202.5 EndY=134 EndZ=0
    g80: LineSegment StartX=-202.5 StartY=134 StartZ=0 EndX=-210.5 EndY=134 EndZ=0
    g81: LineSegment StartX=-210.5 StartY=134 StartZ=0 EndX=-210.5 EndY=164 EndZ=0
    g82: LineSegment StartX=-210.5 StartY=88 StartZ=0 EndX=-202.5 EndY=88 EndZ=0
    g83: LineSegment [constr] StartX=-202.5 StartY=88 StartZ=0 EndX=-202.5 EndY=58 EndZ=0
    g84: LineSegment StartX=-202.5 StartY=58 StartZ=0 EndX=-210.5 EndY=58 EndZ=0
    g85: LineSegment StartX=-210.5 StartY=58 StartZ=0 EndX=-210.5 EndY=88 EndZ=0
    g86: LineSegment StartX=-210.5 StartY=12 StartZ=0 EndX=-202.5 EndY=12 EndZ=0
    g87: LineSegment [constr] StartX=-202.5 StartY=12 StartZ=0 EndX=-202.5 EndY=-18 EndZ=0
    g88: LineSegment StartX=-202.5 StartY=-18 StartZ=0 EndX=-210.5 EndY=-18 EndZ=0
    g89: LineSegment StartX=-210.5 StartY=-18 StartZ=0 EndX=-210.5 EndY=12 EndZ=0
    g90: LineSegment StartX=-210.5 StartY=-64 StartZ=0 EndX=-202.5 EndY=-64 EndZ=0
    g91: LineSegment [constr] StartX=-202.5 StartY=-64 StartZ=0 EndX=-202.5 EndY=-94 EndZ=0
    g92: LineSegment StartX=-202.5 StartY=-94 StartZ=0 EndX=-210.5 EndY=-94 EndZ=0
    g93: LineSegment StartX=-210.5 StartY=-94 StartZ=0 EndX=-210.5 EndY=-64 EndZ=0
    g94: LineSegment StartX=-28.5 StartY=-140 StartZ=0 EndX=28.5 EndY=-140 EndZ=0
    g95: LineSegment StartX=58.5 StartY=-140 StartZ=0 EndX=115.5 EndY=-140 EndZ=0
    g96: LineSegment StartX=145.5 StartY=-140 StartZ=0 EndX=202.5 EndY=-140 EndZ=0
    g97: LineSegment StartX=202.5 StartY=-140 StartZ=0 EndX=202.5 EndY=-94 EndZ=0
    g98: LineSegment StartX=202.5 StartY=-64 StartZ=0 EndX=202.5 EndY=-18 EndZ=0
    g99: LineSegment StartX=202.5 StartY=12 StartZ=0 EndX=202.5 EndY=58 EndZ=0
    g100: LineSegment StartX=202.5 StartY=88 StartZ=0 EndX=202.5 EndY=134 EndZ=0
    g101: LineSegment StartX=202.5 StartY=164 StartZ=0 EndX=202.5 EndY=210 EndZ=0
    g102: LineSegment StartX=145.5 StartY=210 StartZ=0 EndX=202.5 EndY=210 EndZ=0
    g103: LineSegment StartX=58.5 StartY=210 StartZ=0 EndX=115.5 EndY=210 EndZ=0
    g104: LineSegment StartX=-28.5 StartY=210 StartZ=0 EndX=28.5 EndY=210 EndZ=0
    g105: LineSegment StartX=-115.5 StartY=210 StartZ=0 EndX=-58.5 EndY=210 EndZ=0
    g106: LineSegment StartX=-202.5 StartY=210 StartZ=0 EndX=-145.5 EndY=210 EndZ=0
    g107: LineSegment StartX=-202.5 StartY=164 StartZ=0 EndX=-202.5 EndY=210 EndZ=0
    g108: LineSegment StartX=-202.5 StartY=88 StartZ=0 EndX=-202.5 EndY=134 EndZ=0
    g109: LineSegment StartX=-202.5 StartY=12 StartZ=0 EndX=-202.5 EndY=58 EndZ=0
    g110: LineSegment StartX=-202.5 StartY=-64 StartZ=0 EndX=-202.5 EndY=-18 EndZ=0
    g111: LineSegment StartX=-202.5 StartY=-140 StartZ=0 EndX=-202.5 EndY=-94 EndZ=0
    g112: LineSegment StartX=-202.5 StartY=-140 StartZ=0 EndX=-145.5 EndY=-140 EndZ=0
    g113: LineSegment StartX=-115.5 StartY=-140 StartZ=0 EndX=-58.5 EndY=-140 EndZ=0
    g114: LineSegment [constr] StartX=-163.218 StartY=-107.298 StartZ=0 EndX=-159.077 EndY=-91.8431 EndZ=0
    g115: LineSegment [constr] StartX=-159.077 StartY=-91.8431 StartZ=0 EndX=-174.532 EndY=-87.702 EndZ=0
    g116: LineSegment StartX=-174.532 StartY=-87.702 StartZ=0 EndX=-178.673 EndY=-103.157 EndZ=0
    g117: LineSegment StartX=-178.673 StartY=-103.157 StartZ=0 EndX=-163.218 EndY=-107.298 EndZ=0
    g118: Circle [constr] CenterX=-168.875 CenterY=-97.5 CenterZ=0 NormalX=0 NormalY=0 NormalZ=1 AngleXU=0 Radius=11.3137
    g119: LineSegment StartX=163.218 StartY=-107.298 StartZ=0 EndX=178.673 EndY=-103.157 EndZ=0
    g120: LineSegment StartX=178.673 StartY=-103.157 StartZ=0 EndX=174.532 EndY=-87.702 EndZ=0
    g121: LineSegment [constr] StartX=174.532 StartY=-87.702 StartZ=0 EndX=159.077 EndY=-91.8431 EndZ=0
    g122: LineSegment [constr] StartX=159.077 StartY=-91.8431 StartZ=0 EndX=163.218 EndY=-107.298 EndZ=0
    g123: Circle [constr] CenterX=168.875 CenterY=-97.5 CenterZ=0 NormalX=0 NormalY=0 NormalZ=1 AngleXU=0 Radius=11.3137
    g124: LineSegment StartX=11.3137 StartY=195 StartZ=0 EndX=0 EndY=206.314 EndZ=0
    g125: LineSegment StartX=0 StartY=206.314 StartZ=0 EndX=-11.3137 EndY=195 EndZ=0
    g126: LineSegment [constr] StartX=-11.3137 StartY=195 StartZ=0 EndX=0 EndY=183.686 EndZ=0
    g127: LineSegment [constr] StartX=0 StartY=183.686 StartZ=0 EndX=11.3137 EndY=195 EndZ=0
    g128: Circle [constr] CenterX=0 CenterY=195 CenterZ=0 NormalX=0 NormalY=0 NormalZ=1 AngleXU=0 Radius=11.3137
    g129: LineSegment [constr] StartX=-159.631 StartY=-78.8839 StartZ=0 EndX=-148.131 EndY=-98.8024 EndZ=0
    g130: LineSegment StartX=-148.131 StartY=-98.8024 StartZ=0 EndX=-130.81 EndY=-88.8024 EndZ=0
    g131: LineSegment StartX=-130.81 StartY=-88.8024 StartZ=0 EndX=-142.31 EndY=-68.8839 EndZ=0
    g132: LineSegment StartX=-142.31 StartY=-68.8839 StartZ=0 EndX=-159.631 EndY=-78.8839 EndZ=0
    g133: LineSegment [constr] StartX=159.631 StartY=-78.8839 StartZ=0 EndX=148.131 EndY=-98.8024 EndZ=0
    g134: LineSegment StartX=148.131 StartY=-98.8024 StartZ=0 EndX=130.81 EndY=-88.8024 EndZ=0
    g135: LineSegment StartX=130.81 StartY=-88.8024 StartZ=0 EndX=142.31 EndY=-68.8839 EndZ=0
    g136: LineSegment StartX=142.31 StartY=-68.8839 StartZ=0 EndX=159.631 EndY=-78.8839 EndZ=0
    g137: LineSegment [constr] StartX=-11.5 StartY=177.686 StartZ=0 EndX=11.5 EndY=177.686 EndZ=0
    g138: LineSegment StartX=11.5 StartY=177.686 StartZ=0 EndX=11.5 EndY=157.686 EndZ=0
    g139: LineSegment StartX=11.5 StartY=157.686 StartZ=0 EndX=-11.5 EndY=157.686 EndZ=0
    g140: LineSegment StartX=-11.5 StartY=157.686 StartZ=0 EndX=-11.5 EndY=177.686 EndZ=0
    g141: GeomPoint X=-153.881 Y=-88.8431 Z=0
    g142: GeomPoint X=153.881 Y=-88.8431 Z=0
    g143: LineSegment StartX=-174.532 StartY=-87.702 StartZ=0 EndX=-159.631 EndY=-78.8839 EndZ=0
    g144: LineSegment StartX=-163.218 StartY=-107.298 StartZ=0 EndX=-148.131 EndY=-98.8024 EndZ=0
    g145: LineSegment StartX=163.218 StartY=-107.298 StartZ=0 EndX=148.131 EndY=-98.8024 EndZ=0
    g146: LineSegment StartX=159.631 StartY=-78.8839 StartZ=0 EndX=174.532 EndY=-87.702 EndZ=0
    g147: LineSegment StartX=-11.5 StartY=177.686 StartZ=0 EndX=-11.3137 EndY=195 EndZ=0
    g148: LineSegment StartX=11.5 StartY=177.686 StartZ=0 EndX=11.3137 EndY=195 EndZ=0
    g149: Circle CenterX=-193.5 CenterY=-131 CenterZ=0 NormalX=0 NormalY=0 NormalZ=1 AngleXU=0 Radius=1.55
    g150: Circle CenterX=193.5 CenterY=-131 CenterZ=0 NormalX=0 NormalY=0 NormalZ=1 AngleXU=0 Radius=1.55
    g151: Circle CenterX=193.5 CenterY=201 CenterZ=0 NormalX=0 NormalY=0 NormalZ=1 AngleXU=0 Radius=1.55
    g152: Circle CenterX=-193.5 CenterY=201 CenterZ=0 NormalX=0 NormalY=0 NormalZ=1 AngleXU=0 Radius=1.55
  constraints (410):
    c: Coincident(g0,g1)
    c: Coincident(g1,g2)
    c: Coincident(g2,g3)
    c: Coincident(g3,g0)
    c: Horizontal(g0)
    c: Vertical(g3)
    c: Symmetric(g2,g1,g-2)
    c: Symmetric(g0,g1,g-1)
    c: DistanceX(g0,g0) = 220
    c: DistanceY(g1,g1) = 220
    c: Coincident(g8,g9)
    c: Coincident(g9,g10)
    c: Coincident(g10,g11)
    c: Coincident(g11,g8)
    c: Horizontal(g8)
    c: Horizontal(g10)
    c: Vertical(g9)
    c: Vertical(g11)
    c: Coincident(g7,g9)
    c: Coincident(g6,g10)
    c: Coincident(g4,g8)
    c: Coincident(g5,g8)
    c: DistanceY(g4,g0) = 5.5
    c: DistanceX(g0,g4) = 5.5
    c: DistanceX(g5,g0) = 5.5
    c: DistanceY(g2,g6) = 5.5
    c: Radius(g6) = 1.55
    c: Equal(g6,g7)
    c: Equal(g6,g4)
    c: Equal(g6,g5)
    c: Coincident(g12,g13)
    c: Coincident(g12,g14)
    c: Coincident(g12,g-1)
    c: Vertical(g12)
    c: Angle(g13,g12) = 2.0944
    c: Angle(g12,g14) = 2.0944
    c: Equal(g14,g12)
    c: Equal(g12,g13)
    c: DistanceY(g12,g12) = 210
    c: DistanceX(g15,g15) = 66
    c: Symmetric(g15,g15,g12)
    c: DistanceY(g15,g12) = 7.5
    c: Coincident(g15,g17)
    c: Coincident(g15,g16)
    c: Radius(g16) = 2.1
    c: Equal(g16,g17)
    c: Symmetric(g19,g19,g14)
    c: Symmetric(g18,g18,g13)
    c: Distance(g18) = 66
    c: Distance(g19) = 66
    c: PointOnObject(g20,g14)
    c: PointOnObject(g20,g19)
    c: Distance(g14,g20) = 7.5
    c: PointOnObject(g21,g13)
    c: PointOnObject(g21,g18)
    c: Distance(g21,g13) = 7.5
    c: Coincident(g18,g25)
    c: Coincident(g18,g24)
    c: Coincident(g19,g22)
    c: Coincident(g19,g23)
    c: Equal(g23,g22)
    c: Equal(g22,g24)
    c: Equal(g24,g25)
    c: Equal(g25,g17)
    c: Coincident(g26,g27)
    c: Coincident(g27,g28)
    c: Coincident(g28,g29)
    c: Coincident(g29,g26)
    c: Horizontal(g28)
    c: Vertical(g27)
    c: Vertical(g29)
    c: DistanceY(g16,g28) = 7.5
    c: Coincident(g30,g31)
    c: Coincident(g31,g32)
    c: Coincident(g32,g33)
    c: Coincident(g33,g30)
    c: Horizontal(g30)
    c: Horizontal(g32)
    c: Vertical(g31)
    c: Vertical(g33)
    c: Coincident(g34,g35)
    c: Coincident(g35,g36)
    c: Coincident(g36,g37)
    c: Coincident(g37,g34)
    c: Horizontal(g34)
    c: Horizontal(g36)
    c: Vertical(g35)
    c: Vertical(g37)
    c: Coincident(g38,g39)
    c: Coincident(g39,g40)
    c: Coincident(g40,g41)
    c: Coincident(g41,g38)
    c: Horizontal(g38)
    c: Horizontal(g40)
    c: Vertical(g39)
    c: Vertical(g41)
    c: Coincident(g42,g43)
    c: Coincident(g43,g44)
    c: Coincident(g44,g45)
    c: Coincident(g45,g42)
    c: Horizontal(g42)
    c: Horizontal(g44)
    c: Vertical(g43)
    c: Vertical(g45)
    c: Coincident(g46,g47)
    c: Coincident(g47,g48)
    c: Coincident(g48,g49)
    c: Coincident(g49,g46)
    c: Horizontal(g46)
    c: Horizontal(g48)
    c: Vertical(g47)
    c: Vertical(g49)
    c: Coincident(g50,g51)
    c: Coincident(g51,g52)
    c: Coincident(g52,g53)
    c: Coincident(g53,g50)
    c: Horizontal(g50)
    c: Horizontal(g52)
    c: Vertical(g51)
    c: Vertical(g53)
    c: Coincident(g54,g55)
    c: Coincident(g55,g56)
    c: Coincident(g56,g57)
    c: Coincident(g57,g54)
    c: Horizontal(g54)
    c: Horizontal(g56)
    c: Vertical(g55)
    c: Vertical(g57)
    c: Coincident(g58,g59)
    c: Coincident(g59,g60)
    c: Coincident(g60,g61)
    c: Coincident(g61,g58)
    c: Horizontal(g58)
    c: Horizontal(g60)
    c: Vertical(g59)
    c: Vertical(g61)
    c: Coincident(g62,g63)
    c: Coincident(g63,g64)
    c: Coincident(g64,g65)
    c: Coincident(g65,g62)
    c: Horizontal(g62)
    c: Horizontal(g64)
    c: Vertical(g63)
    c: Vertical(g65)
    c: Coincident(g66,g67)
    c: Coincident(g67,g68)
    c: Coincident(g68,g69)
    c: Coincident(g69,g66)
    c: Horizontal(g66)
    c: Horizontal(g68)
    c: Vertical(g67)
    c: Vertical(g69)
    c: Coincident(g70,g71)
    c: Coincident(g71,g72)
    c: Coincident(g72,g73)
    c: Coincident(g73,g70)
    c: Horizontal(g70)
    c: Horizontal(g72)
    c: Vertical(g71)
    c: Vertical(g73)
    c: Coincident(g74,g75)
    c: Coincident(g75,g76)
    c: Coincident(g76,g77)
    c: Coincident(g77,g74)
    c: Horizontal(g74)
    c: Horizontal(g76)
    c: Vertical(g75)
    c: Vertical(g77)
    c: Coincident(g78,g79)
    c: Coincident(g79,g80)
    c: Coincident(g80,g81)
    c: Coincident(g81,g78)
    c: Horizontal(g78)
    c: Horizontal(g80)
    c: Vertical(g79)
    c: Vertical(g81)
    c: Coincident(g82,g83)
    c: Coincident(g83,g84)
    c: Coincident(g84,g85)
    c: Coincident(g85,g82)
    c: Horizontal(g82)
    c: Horizontal(g84)
    c: Vertical(g83)
    c: Vertical(g85)
    c: Coincident(g86,g87)
    c: Coincident(g87,g88)
    c: Coincident(g88,g89)
    c: Coincident(g89,g86)
    c: Horizontal(g86)
    c: Horizontal(g88)
    c: Vertical(g87)
    c: Vertical(g89)
    c: Coincident(g91,g92)
    c: Coincident(g92,g93)
    c: Coincident(g93,g90)
    c: Horizontal(g90)
    c: Horizontal(g92)
    c: Vertical(g91)
    c: Vertical(g93)
    c: PointOnObject(g34,g26)
    c: PointOnObject(g30,g26)
    c: PointOnObject(g91,g29)
    c: PointOnObject(g87,g29)
    c: PointOnObject(g83,g29)
    c: PointOnObject(g79,g29)
    c: PointOnObject(g64,g28)
    c: PointOnObject(g68,g28)
    c: PointOnObject(g72,g28)
    c: PointOnObject(g76,g28)
    c: PointOnObject(g60,g27)
    c: PointOnObject(g56,g27)
    c: PointOnObject(g52,g27)
    c: PointOnObject(g48,g27)
    c: PointOnObject(g42,g26)
    c: PointOnObject(g38,g26)
    c: Equal(g39,g45)
    c: Equal(g45,g48)
    c: Equal(g48,g52)
    c: Equal(g52,g56)
    c: Equal(g56,g60)
    c: Equal(g60,g75)
    c: Equal(g75,g71)
    c: Equal(g71,g67)
    c: Equal(g67,g63)
    c: Equal(g63,g78)
    c: Equal(g78,g82)
    c: Equal(g82,g86)
    c: Equal(g86,g90)
    c: Equal(g90,g33)
    c: Equal(g33,g37)
    c: DistanceY(g65,g65) = 8
    c: Equal(g32,g36)
    c: Equal(g36,g40)
    c: Equal(g40,g44)
    c: Equal(g44,g47)
    c: Equal(g47,g51)
    c: Equal(g51,g55)
    c: Equal(g55,g59)
    c: Equal(g59,g74)
    c: Equal(g74,g70)
    c: Equal(g70,g66)
    c: Equal(g66,g62)
    c: Equal(g62,g81)
    c: Equal(g81,g85)
    c: Equal(g85,g89)
    c: Equal(g89,g93)
    c: DistanceX(g62,g62) = 30
    c: Coincident(g113,g30)
    c: Coincident(g113,g34)
    c: Coincident(g34,g94)
    c: Coincident(g38,g94)
    c: Coincident(g38,g95)
    c: Coincident(g42,g95)
    c: Coincident(g96,g42)
    c: Coincident(g26,g96)
    c: Coincident(g26,g97)
    c: Coincident(g48,g97)
    c: Coincident(g46,g98)
    c: Coincident(g52,g98)
    c: Coincident(g50,g99)
    c: Coincident(g56,g99)
    c: Coincident(g54,g100)
    c: Coincident(g60,g100)
    c: Coincident(g58,g101)
    c: Coincident(g27,g101)
    c: Coincident(g27,g102)
    c: Coincident(g75,g102)
    c: Coincident(g76,g103)
    c: Coincident(g71,g103)
    c: Coincident(g72,g104)
    c: Coincident(g67,g104)
    c: Coincident(g68,g105)
    c: Coincident(g63,g105)
    c: Coincident(g64,g106)
    c: Coincident(g28,g106)
    c: Coincident(g28,g107)
    c: Coincident(g78,g107)
    c: Coincident(g82,g108)
    c: Coincident(g79,g108)
    c: Coincident(g86,g109)
    c: Coincident(g83,g109)
    c: Coincident(g87,g110)
    c: Coincident(g91,g111)
    c: Coincident(g26,g111)
    c: Coincident(g26,g112)
    c: Coincident(g30,g112)
    c: Equal(g97,g98)
    c: Equal(g98,g99)
    c: Equal(g99,g100)
    c: Equal(g100,g101)
    c: Equal(g106,g105)
    c: Equal(g105,g104)
    c: Equal(g104,g103)
    c: Equal(g103,g102)
    c: Equal(g107,g108)
    c: Equal(g108,g109)
    c: Equal(g109,g110)
    c: Equal(g110,g111)
    c: Equal(g112,g113)
    c: Equal(g113,g94)
    c: Equal(g94,g95)
    c: Equal(g95,g96)
    c: Coincident(g114,g115)
    c: Coincident(g115,g116)
    c: Coincident(g116,g117)
    c: Coincident(g117,g114)
    c: Equal(g114,g115)
    c: Equal(g114,g116)
    c: Equal(g114,g117)
    c: PointOnObject(g114,g118)
    c: PointOnObject(g115,g118)
    c: PointOnObject(g116,g118)
    c: PointOnObject(g117,g118)
    c: Coincident(g119,g120)
    c: Coincident(g120,g121)
    c: Coincident(g121,g122)
    c: Coincident(g122,g119)
    c: Equal(g119,g120)
    c: Equal(g119,g121)
    c: Equal(g119,g122)
    c: PointOnObject(g119,g123)
    c: PointOnObject(g120,g123)
    c: PointOnObject(g121,g123)
    c: PointOnObject(g122,g123)
    c: Coincident(g124,g125)
    c: Coincident(g125,g126)
    c: Coincident(g126,g127)
    c: Coincident(g127,g124)
    c: Equal(g124,g125)
    c: Equal(g124,g126)
    c: Equal(g124,g127)
    c: PointOnObject(g124,g128)
    c: PointOnObject(g125,g128)
    c: PointOnObject(g126,g128)
    c: PointOnObject(g127,g128)
    c: PointOnObject(g128,g12)
    c: PointOnObject(g118,g14)
    c: PointOnObject(g123,g13)
    c: PointOnObject(g121,g13)
    c: PointOnObject(g114,g14)
    c: PointOnObject(g126,g12)
    c: Distance(g125) = 16
    c: Equal(g128,g118)
    c: Equal(g118,g123)
    c: DistanceY(g128,g12) = 15
    c: Distance(g118,g14) = 15
    c: Coincident(g129,g130)
    c: Coincident(g130,g131)
    c: Coincident(g131,g132)
    c: Coincident(g129,g132)
    c: Coincident(g133,g134)
    c: Coincident(g134,g135)
    c: Coincident(g135,g136)
    c: Coincident(g133,g136)
    c: Coincident(g137,g138)
    c: Coincident(g138,g139)
    c: Coincident(g139,g140)
    c: Coincident(g137,g140)
    c: Symmetric(g133,g133,g13)
    c: Equal(g135,g133)
    c: Symmetric(g135,g134,g13)
    c: Symmetric(g129,g129,g14)
    c: Symmetric(g130,g131,g14)
    c: Equal(g131,g129)
    c: Symmetric(g137,g137,g12)
    c: Symmetric(g139,g138,g12)
    c: Equal(g137,g139)
    c: Equal(g137,g135)
    c: Equal(g135,g131)
    c: Equal(g138,g136)
    c: Equal(g136,g132)
    c: PointOnObject(g141,g14)
    c: PointOnObject(g141,g129)
    c: Distance(g141,g114) = 6
    c: PointOnObject(g142,g13)
    c: PointOnObject(g142,g133)
    c: Distance(g142,g121) = 6
    c: DistanceY(g137,g126) = 6
    c: DistanceY(g138,g138) = 20
    c: DistanceX(g137,g137) = 23
    c: DistanceX(g111,g96) = 405
    c: DistanceY(g96,g101) = 350
    c: Symmetric(g111,g96,g-2)
    c: Coincident(g90,g110)
    c: Coincident(g90,g91)
    c: Coincident(g129,g144)
    c: Coincident(g129,g143)
    c: Coincident(g114,g144)
    c: Coincident(g115,g143)
    c: Coincident(g120,g146)
    c: Coincident(g133,g146)
    c: Coincident(g133,g145)
    c: Coincident(g119,g145)
    c: Coincident(g124,g148)
    c: Coincident(g137,g148)
    c: Coincident(g137,g147)
    c: Coincident(g125,g147)
    c: DistanceX(g111,g149) = 9
    c: DistanceY(g111,g149) = 9
    c: Radius(g149) = 1.55
    c: DistanceX(g150,g96) = 9
    c: DistanceY(g96,g150) = 9
    c: Radius(g150) = 1.55
    c: DistanceX(g151,g101) = 9
    c: DistanceY(g151,g101) = 9
    c: Radius(g151) = 1.55
    c: DistanceX(g106,g152) = 9
    c: DistanceY(g152,g106) = 9
    c: Radius(g152) = 1.55
    c: Distance(g123,g13) = 15
FEATURE [Sketcher::SketchObject] Sketch002  label="top2"
  sketch-geometry (4):
    g0: LineSegment StartX=-210.5 StartY=219 StartZ=0 EndX=210.5 EndY=219 EndZ=0
    g1: LineSegment StartX=210.5 StartY=219 StartZ=0 EndX=210.5 EndY=-147 EndZ=0
    g2: LineSegment StartX=210.5 StartY=-147 StartZ=0 EndX=-210.5 EndY=-147 EndZ=0
    g3: LineSegment StartX=-210.5 StartY=-147 StartZ=0 EndX=-210.5 EndY=219 EndZ=0
  constraints (10):
    c: Coincident(g0,g1)
    c: Coincident(g1,g2)
    c: Coincident(g2,g3)
    c: Coincident(g3,g0)
    c: Horizontal(g2)
    c: Vertical(g3)
    c: Symmetric(g0,g0,g-2)
    c: DistanceX(g0,g0) = 421
    c: DistanceY(g1,g1) = 366
    c: DistanceY(g-1,g0) = 219
FEATURE [Sketcher::SketchObject] Sketch003  label="left_right"
  sketch-geometry (148):
    g0: LineSegment StartX=-183 StartY=329 StartZ=0 EndX=183 EndY=329 EndZ=0
    g1: LineSegment [constr] StartX=183 StartY=329 StartZ=0 EndX=183 EndY=-329 EndZ=0
    g2: LineSegment StartX=183 StartY=-329 StartZ=0 EndX=-183 EndY=-329 EndZ=0
    g3: LineSegment [constr] StartX=-183 StartY=-329 StartZ=0 EndX=-183 EndY=329 EndZ=0
    g4: LineSegment StartX=-183 StartY=290.2 StartZ=0 EndX=-175 EndY=290.2 EndZ=0
    g5: LineSegment StartX=-175 StartY=290.2 StartZ=0 EndX=-175 EndY=260.2 EndZ=0
    g6: LineSegment StartX=-175 StartY=260.2 StartZ=0 EndX=-183 EndY=260.2 EndZ=0
    g7: LineSegment [constr] StartX=-183 StartY=260.2 StartZ=0 EndX=-183 EndY=290.2 EndZ=0
    g8: LineSegment StartX=-183 StartY=221.4 StartZ=0 EndX=-175 EndY=221.4 EndZ=0
    g9: LineSegment StartX=-175 StartY=221.4 StartZ=0 EndX=-175 EndY=191.4 EndZ=0
    g10: LineSegment StartX=-175 StartY=191.4 StartZ=0 EndX=-183 EndY=191.4 EndZ=0
    g11: LineSegment [constr] StartX=-183 StartY=191.4 StartZ=0 EndX=-183 EndY=221.4 EndZ=0
    g12: LineSegment StartX=-183 StartY=152.6 StartZ=0 EndX=-175 EndY=152.6 EndZ=0
    g13: LineSegment StartX=-175 StartY=152.6 StartZ=0 EndX=-175 EndY=122.6 EndZ=0
    g14: LineSegment StartX=-175 StartY=122.6 StartZ=0 EndX=-183 EndY=122.6 EndZ=0
    g15: LineSegment [constr] StartX=-183 StartY=122.6 StartZ=0 EndX=-183 EndY=152.6 EndZ=0
    g16: LineSegment StartX=-183 StartY=83.8 StartZ=0 EndX=-175 EndY=83.8 EndZ=0
    g17: LineSegment StartX=-175 StartY=83.8 StartZ=0 EndX=-175 EndY=53.8 EndZ=0
    g18: LineSegment StartX=-175 StartY=53.8 StartZ=0 EndX=-183 EndY=53.8 EndZ=0
    g19: LineSegment [constr] StartX=-183 StartY=53.8 StartZ=0 EndX=-183 EndY=83.8 EndZ=0
    g20: LineSegment StartX=-183 StartY=15 StartZ=0 EndX=-175 EndY=15 EndZ=0
    g21: LineSegment StartX=-175 StartY=15 StartZ=0 EndX=-175 EndY=-15 EndZ=0
    g22: LineSegment StartX=-175 StartY=-15 StartZ=0 EndX=-183 EndY=-15 EndZ=0
    g23: LineSegment [constr] StartX=-183 StartY=-15 StartZ=0 EndX=-183 EndY=15 EndZ=0
    g24: LineSegment StartX=-183 StartY=-53.8 StartZ=0 EndX=-175 EndY=-53.8 EndZ=0
    g25: LineSegment StartX=-175 StartY=-53.8 StartZ=0 EndX=-175 EndY=-83.8 EndZ=0
    g26: LineSegment StartX=-175 StartY=-83.8 StartZ=0 EndX=-183 EndY=-83.8 EndZ=0
    g27: LineSegment [constr] StartX=-183 StartY=-83.8 StartZ=0 EndX=-183 EndY=-53.8 EndZ=0
    g28: LineSegment StartX=-183 StartY=-122.6 StartZ=0 EndX=-175 EndY=-122.6 EndZ=0
    g29: LineSegment StartX=-175 StartY=-122.6 StartZ=0 EndX=-175 EndY=-152.6 EndZ=0
    g30: LineSegment StartX=-175 StartY=-152.6 StartZ=0 EndX=-183 EndY=-152.6 EndZ=0
    g31: LineSegment [constr] StartX=-183 StartY=-152.6 StartZ=0 EndX=-183 EndY=-122.6 EndZ=0
    g32: LineSegment StartX=-183 StartY=-191.4 StartZ=0 EndX=-175 EndY=-191.4 EndZ=0
    g33: LineSegment StartX=-175 StartY=-191.4 StartZ=0 EndX=-175 EndY=-221.4 EndZ=0
    g34: LineSegment StartX=-175 StartY=-221.4 StartZ=0 EndX=-183 EndY=-221.4 EndZ=0
    g35: LineSegment [constr] StartX=-183 StartY=-221.4 StartZ=0 EndX=-183 EndY=-191.4 EndZ=0
    g36: LineSegment StartX=-183 StartY=-260.2 StartZ=0 EndX=-175 EndY=-260.2 EndZ=0
    g37: LineSegment StartX=-175 StartY=-260.2 StartZ=0 EndX=-175 EndY=-290.2 EndZ=0
    g38: LineSegment StartX=-175 StartY=-290.2 StartZ=0 EndX=-183 EndY=-290.2 EndZ=0
    g39: LineSegment [constr] StartX=-183 StartY=-290.2 StartZ=0 EndX=-183 EndY=-260.2 EndZ=0
    g40: LineSegment StartX=183 StartY=-260.2 StartZ=0 EndX=175 EndY=-260.2 EndZ=0
    g41: LineSegment StartX=175 StartY=-260.2 StartZ=0 EndX=175 EndY=-290.2 EndZ=0
    g42: LineSegment StartX=175 StartY=-290.2 StartZ=0 EndX=183 EndY=-290.2 EndZ=0
    g43: LineSegment [constr] StartX=183 StartY=-290.2 StartZ=0 EndX=183 EndY=-260.2 EndZ=0
    g44: LineSegment StartX=183 StartY=-191.4 StartZ=0 EndX=175 EndY=-191.4 EndZ=0
    g45: LineSegment StartX=175 StartY=-191.4 StartZ=0 EndX=175 EndY=-221.4 EndZ=0
    g46: LineSegment StartX=175 StartY=-221.4 StartZ=0 EndX=183 EndY=-221.4 EndZ=0
    g47: LineSegment [constr] StartX=183 StartY=-221.4 StartZ=0 EndX=183 EndY=-191.4 EndZ=0
    g48: LineSegment StartX=183 StartY=-122.6 StartZ=0 EndX=175 EndY=-122.6 EndZ=0
    g49: LineSegment StartX=175 StartY=-122.6 StartZ=0 EndX=175 EndY=-152.6 EndZ=0
    g50: LineSegment StartX=175 StartY=-152.6 StartZ=0 EndX=183 EndY=-152.6 EndZ=0
    g51: LineSegment [constr] StartX=183 StartY=-152.6 StartZ=0 EndX=183 EndY=-122.6 EndZ=0
    g52: LineSegment StartX=183 StartY=-53.8 StartZ=0 EndX=175 EndY=-53.8 EndZ=0
    g53: LineSegment StartX=175 StartY=-53.8 StartZ=0 EndX=175 EndY=-83.8 EndZ=0
    g54: LineSegment StartX=175 StartY=-83.8 StartZ=0 EndX=183 EndY=-83.8 EndZ=0
    g55: LineSegment [constr] StartX=183 StartY=-83.8 StartZ=0 EndX=183 EndY=-53.8 EndZ=0
    g56: LineSegment StartX=183 StartY=15 StartZ=0 EndX=175 EndY=15 EndZ=0
    g57: LineSegment StartX=175 StartY=15 StartZ=0 EndX=175 EndY=-15 EndZ=0
    g58: LineSegment StartX=175 StartY=-15 StartZ=0 EndX=183 EndY=-15 EndZ=0
    g59: LineSegment [constr] StartX=183 StartY=-15 StartZ=0 EndX=183 EndY=15 EndZ=0
    g60: LineSegment StartX=183 StartY=83.8 StartZ=0 EndX=175 EndY=83.8 EndZ=0
    g61: LineSegment StartX=175 StartY=83.8 StartZ=0 EndX=175 EndY=53.8 EndZ=0
    g62: LineSegment StartX=175 StartY=53.8 StartZ=0 EndX=183 EndY=53.8 EndZ=0
    g63: LineSegment [constr] StartX=183 StartY=53.8 StartZ=0 EndX=183 EndY=83.8 EndZ=0
    g64: LineSegment StartX=183 StartY=152.6 StartZ=0 EndX=175 EndY=152.6 EndZ=0
    g65: LineSegment StartX=175 StartY=152.6 StartZ=0 EndX=175 EndY=122.6 EndZ=0
    g66: LineSegment StartX=175 StartY=122.6 StartZ=0 EndX=183 EndY=122.6 EndZ=0
    g67: LineSegment [constr] StartX=183 StartY=122.6 StartZ=0 EndX=183 EndY=152.6 EndZ=0
    g68: LineSegment StartX=183 StartY=221.4 StartZ=0 EndX=175 EndY=221.4 EndZ=0
    g69: LineSegment StartX=175 StartY=221.4 StartZ=0 EndX=175 EndY=191.4 EndZ=0
    g70: LineSegment StartX=175 StartY=191.4 StartZ=0 EndX=183 EndY=191.4 EndZ=0
    g71: LineSegment [constr] StartX=183 StartY=191.4 StartZ=0 EndX=183 EndY=221.4 EndZ=0
    g72: LineSegment StartX=183 StartY=290.2 StartZ=0 EndX=175 EndY=290.2 EndZ=0
    g73: LineSegment StartX=175 StartY=290.2 StartZ=0 EndX=175 EndY=260.2 EndZ=0
    g74: LineSegment StartX=175 StartY=260.2 StartZ=0 EndX=183 EndY=260.2 EndZ=0
    g75: LineSegment [constr] StartX=183 StartY=260.2 StartZ=0 EndX=183 EndY=290.2 EndZ=0
    g76: LineSegment StartX=183 StartY=290.2 StartZ=0 EndX=183 EndY=329 EndZ=0
    g77: LineSegment StartX=183 StartY=221.4 StartZ=0 EndX=183 EndY=260.2 EndZ=0
    g78: LineSegment StartX=183 StartY=152.6 StartZ=0 EndX=183 EndY=191.4 EndZ=0
    g79: LineSegment StartX=183 StartY=83.8 StartZ=0 EndX=183 EndY=122.6 EndZ=0
    g80: LineSegment StartX=183 StartY=15 StartZ=0 EndX=183 EndY=53.8 EndZ=0
    g81: LineSegment StartX=183 StartY=-53.8 StartZ=0 EndX=183 EndY=-15 EndZ=0
    g82: LineSegment StartX=183 StartY=-122.6 StartZ=0 EndX=183 EndY=-83.8 EndZ=0
    g83: LineSegment StartX=183 StartY=-191.4 StartZ=0 EndX=183 EndY=-152.6 EndZ=0
    g84: LineSegment StartX=183 StartY=-260.2 StartZ=0 EndX=183 EndY=-221.4 EndZ=0
    g85: LineSegment StartX=183 StartY=-329 StartZ=0 EndX=183 EndY=-290.2 EndZ=0
    g86: LineSegment StartX=-183 StartY=290.2 StartZ=0 EndX=-183 EndY=329 EndZ=0
    g87: LineSegment StartX=-183 StartY=221.4 StartZ=0 EndX=-183 EndY=260.2 EndZ=0
    g88: LineSegment StartX=-183 StartY=152.6 StartZ=0 EndX=-183 EndY=191.4 EndZ=0
    g89: LineSegment StartX=-183 StartY=83.8 StartZ=0 EndX=-183 EndY=122.6 EndZ=0
    g90: LineSegment StartX=-183 StartY=15 StartZ=0 EndX=-183 EndY=53.8 EndZ=0
    g91: LineSegment StartX=-183 StartY=-53.8 StartZ=0 EndX=-183 EndY=-15 EndZ=0
    g92: LineSegment StartX=-183 StartY=-122.6 StartZ=0 EndX=-183 EndY=-83.8 EndZ=0
    g93: LineSegment StartX=-183 StartY=-191.4 StartZ=0 EndX=-183 EndY=-152.6 EndZ=0
    g94: LineSegment StartX=-183 StartY=-260.2 StartZ=0 EndX=-183 EndY=-221.4 EndZ=0
    g95: LineSegment StartX=-183 StartY=-329 StartZ=0 EndX=-183 EndY=-290.2 EndZ=0
    g96: ArcOfCircle CenterX=-25 CenterY=289 CenterZ=0 NormalX=0 NormalY=0 NormalZ=1 AngleXU=0 Radius=15 StartAngle=1.5708 EndAngle=4.71239
    g97: ArcOfCircle CenterX=25 CenterY=289 CenterZ=0 NormalX=0 NormalY=0 NormalZ=1 AngleXU=0 Radius=15 StartAngle=4.71239 EndAngle=7.85398
    g98: LineSegment StartX=-25 StartY=274 StartZ=0 EndX=25 EndY=274 EndZ=0
    g99: LineSegment StartX=-25 StartY=304 StartZ=0 EndX=25 EndY=304 EndZ=0
    g100: LineSegment StartX=-129 StartY=249 StartZ=0 EndX=-99 EndY=249 EndZ=0
    g101: LineSegment StartX=-99 StartY=249 StartZ=0 EndX=-99 EndY=241 EndZ=0
    g102: LineSegment StartX=-99 StartY=241 StartZ=0 EndX=-129 EndY=241 EndZ=0
    g103: LineSegment StartX=-129 StartY=241 StartZ=0 EndX=-129 EndY=249 EndZ=0
    g104: LineSegment StartX=-53 StartY=249 StartZ=0 EndX=-23 EndY=249 EndZ=0
    g105: LineSegment StartX=-23 StartY=249 StartZ=0 EndX=-23 EndY=241 EndZ=0
    g106: LineSegment StartX=-23 StartY=241 StartZ=0 EndX=-53 EndY=241 EndZ=0
    g107: LineSegment StartX=-53 StartY=241 StartZ=0 EndX=-53 EndY=249 EndZ=0
    g108: LineSegment StartX=23 StartY=249 StartZ=0 EndX=53 EndY=249 EndZ=0
    g109: LineSegment StartX=53 StartY=249 StartZ=0 EndX=53 EndY=241 EndZ=0
    g110: LineSegment StartX=53 StartY=241 StartZ=0 EndX=23 EndY=241 EndZ=0
    g111: LineSegment StartX=23 StartY=241 StartZ=0 EndX=23 EndY=249 EndZ=0
    g112: LineSegment StartX=99 StartY=249 StartZ=0 EndX=129 EndY=249 EndZ=0
    g113: LineSegment StartX=129 StartY=249 StartZ=0 EndX=129 EndY=241 EndZ=0
    g114: LineSegment StartX=129 StartY=241 StartZ=0 EndX=99 EndY=241 EndZ=0
    g115: LineSegment StartX=99 StartY=241 StartZ=0 EndX=99 EndY=249 EndZ=0
    g116: LineSegment [constr] StartX=-175 StartY=241 StartZ=0 EndX=-129 EndY=241 EndZ=0
    g117: LineSegment [constr] StartX=-99 StartY=241 StartZ=0 EndX=-53 EndY=241 EndZ=0
    g118: LineSegment [constr] StartX=-23 StartY=241 StartZ=0 EndX=23 EndY=241 EndZ=0
    g119: LineSegment [constr] StartX=53 StartY=241 StartZ=0 EndX=99 EndY=241 EndZ=0
    g120: LineSegment [constr] StartX=129 StartY=241 StartZ=0 EndX=175 EndY=241 EndZ=0
    g121: LineSegment StartX=-129 StartY=-311 StartZ=0 EndX=-99 EndY=-311 EndZ=0
    g122: LineSegment StartX=-99 StartY=-311 StartZ=0 EndX=-99 EndY=-319 EndZ=0
    g123: LineSegment StartX=-99 StartY=-319 StartZ=0 EndX=-129 EndY=-319 EndZ=0
    g124: LineSegment StartX=-129 StartY=-319 StartZ=0 EndX=-129 EndY=-311 EndZ=0
    g125: LineSegment StartX=-53 StartY=-311 StartZ=0 EndX=-23 EndY=-311 EndZ=0
    g126: LineSegment StartX=-23 StartY=-311 StartZ=0 EndX=-23 EndY=-319 EndZ=0
    g127: LineSegment StartX=-23 StartY=-319 StartZ=0 EndX=-53 EndY=-319 EndZ=0
    g128: LineSegment StartX=-53 StartY=-319 StartZ=0 EndX=-53 EndY=-311 EndZ=0
    g129: LineSegment StartX=23 StartY=-311 StartZ=0 EndX=53 EndY=-311 EndZ=0
    g130: LineSegment StartX=53 StartY=-311 StartZ=0 EndX=53 EndY=-319 EndZ=0
    g131: LineSegment StartX=53 StartY=-319 StartZ=0 EndX=23 EndY=-319 EndZ=0
    g132: LineSegment StartX=23 StartY=-319 StartZ=0 EndX=23 EndY=-311 EndZ=0
    g133: LineSegment StartX=99 StartY=-311 StartZ=0 EndX=129 EndY=-311 EndZ=0
    g134: LineSegment StartX=129 StartY=-311 StartZ=0 EndX=129 EndY=-319 EndZ=0
    g135: LineSegment StartX=129 StartY=-319 StartZ=0 EndX=99 EndY=-319 EndZ=0
    g136: LineSegment StartX=99 StartY=-319 StartZ=0 EndX=99 EndY=-311 EndZ=0
    g137: LineSegment [constr] StartX=-99 StartY=-319 StartZ=0 EndX=-53 EndY=-319 EndZ=0
    g138: LineSegment [constr] StartX=-23 StartY=-319 StartZ=0 EndX=23 EndY=-319 EndZ=0
    g139: LineSegment [constr] StartX=53 StartY=-319 StartZ=0 EndX=99 EndY=-319 EndZ=0
    g140: LineSegment [constr] StartX=-175 StartY=-319 StartZ=0 EndX=-129 EndY=-319 EndZ=0
    g141: LineSegment [constr] StartX=129 StartY=-319 StartZ=0 EndX=175 EndY=-319 EndZ=0
    g142: Circle CenterX=-165 CenterY=-306 CenterZ=0 NormalX=0 NormalY=0 NormalZ=1 AngleXU=0 Radius=1.55
    g143: Circle CenterX=165 CenterY=-306 CenterZ=0 NormalX=0 NormalY=0 NormalZ=1 AngleXU=0 Radius=1.55
    g144: Circle CenterX=-165 CenterY=-10 CenterZ=0 NormalX=0 NormalY=0 NormalZ=1 AngleXU=0 Radius=1.55
    g145: Circle CenterX=165 CenterY=-10 CenterZ=0 NormalX=0 NormalY=0 NormalZ=1 AngleXU=0 Radius=1.55
    g146: Circle CenterX=-165 CenterY=254 CenterZ=0 NormalX=0 NormalY=0 NormalZ=1 AngleXU=0 Radius=1.55
    g147: Circle CenterX=165 CenterY=254 CenterZ=0 NormalX=0 NormalY=0 NormalZ=1 AngleXU=0 Radius=1.55
  constraints (413):
    c: Coincident(g0,g1)
    c: Coincident(g1,g2)
    c: Coincident(g2,g3)
    c: Coincident(g3,g0)
    c: Horizontal(g0)
    c: Vertical(g1)
    c: Symmetric(g1,g2,g-2)
    c: DistanceX(g0,g0) = 366
    c: DistanceY(g1,g1) = 658
    c: Coincident(g4,g5)
    c: Coincident(g5,g6)
    c: Coincident(g6,g7)
    c: Coincident(g7,g4)
    c: Horizontal(g4)
    c: Horizontal(g6)
    c: Vertical(g5)
    c: Vertical(g7)
    c: Coincident(g8,g9)
    c: Coincident(g9,g10)
    c: Coincident(g10,g11)
    c: Coincident(g11,g8)
    c: Horizontal(g8)
    c: Horizontal(g10)
    c: Vertical(g9)
    c: Vertical(g11)
    c: Coincident(g12,g13)
    c: Coincident(g13,g14)
    c: Coincident(g14,g15)
    c: Coincident(g15,g12)
    c: Horizontal(g12)
    c: Horizontal(g14)
    c: Vertical(g13)
    c: Vertical(g15)
    c: Coincident(g16,g17)
    c: Coincident(g17,g18)
    c: Coincident(g18,g19)
    c: Coincident(g19,g16)
    c: Horizontal(g16)
    c: Horizontal(g18)
    c: Vertical(g17)
    c: Vertical(g19)
    c: Coincident(g20,g21)
    c: Coincident(g21,g22)
    c: Coincident(g22,g23)
    c: Coincident(g23,g20)
    c: Horizontal(g20)
    c: Horizontal(g22)
    c: Vertical(g21)
    c: Vertical(g23)
    c: Coincident(g24,g25)
    c: Coincident(g25,g26)
    c: Coincident(g26,g27)
    c: Coincident(g27,g24)
    c: Horizontal(g24)
    c: Horizontal(g26)
    c: Vertical(g25)
    c: Vertical(g27)
    c: Coincident(g28,g29)
    c: Coincident(g29,g30)
    c: Coincident(g30,g31)
    c: Coincident(g31,g28)
    c: Horizontal(g28)
    c: Horizontal(g30)
    c: Vertical(g29)
    c: Vertical(g31)
    c: Coincident(g32,g33)
    c: Coincident(g33,g34)
    c: Coincident(g34,g35)
    c: Coincident(g35,g32)
    c: Horizontal(g32)
    c: Horizontal(g34)
    c: Vertical(g33)
    c: Vertical(g35)
    c: Coincident(g36,g37)
    c: Coincident(g37,g38)
    c: Coincident(g38,g39)
    c: Coincident(g39,g36)
    c: Horizontal(g36)
    c: Horizontal(g38)
    c: Vertical(g37)
    c: Vertical(g39)
    c: Coincident(g40,g41)
    c: Coincident(g41,g42)
    c: Coincident(g42,g43)
    c: Coincident(g43,g40)
    c: Horizontal(g40)
    c: Horizontal(g42)
    c: Vertical(g41)
    c: Vertical(g43)
    c: Coincident(g44,g45)
    c: Coincident(g45,g46)
    c: Coincident(g46,g47)
    c: Coincident(g47,g44)
    c: Horizontal(g44)
    c: Horizontal(g46)
    c: Vertical(g45)
    c: Vertical(g47)
    c: Coincident(g48,g49)
    c: Coincident(g49,g50)
    c: Coincident(g50,g51)
    c: Coincident(g51,g48)
    c: Horizontal(g48)
    c: Horizontal(g50)
    c: Vertical(g49)
    c: Vertical(g51)
    c: Coincident(g52,g53)
    c: Coincident(g53,g54)
    c: Coincident(g54,g55)
    c: Coincident(g55,g52)
    c: Horizontal(g52)
    c: Horizontal(g54)
    c: Vertical(g53)
    c: Vertical(g55)
    c: Coincident(g56,g57)
    c: Coincident(g57,g58)
    c: Coincident(g58,g59)
    c: Coincident(g59,g56)
    c: Horizontal(g56)
    c: Horizontal(g58)
    c: Vertical(g57)
    c: Vertical(g59)
    c: Coincident(g60,g61)
    c: Coincident(g61,g62)
    c: Coincident(g62,g63)
    c: Coincident(g63,g60)
    c: Horizontal(g60)
    c: Horizontal(g62)
    c: Vertical(g61)
    c: Vertical(g63)
    c: Coincident(g64,g65)
    c: Coincident(g65,g66)
    c: Coincident(g66,g67)
    c: Coincident(g67,g64)
    c: Horizontal(g64)
    c: Horizontal(g66)
    c: Vertical(g65)
    c: Vertical(g67)
    c: Coincident(g68,g69)
    c: Coincident(g69,g70)
    c: Coincident(g70,g71)
    c: Coincident(g71,g68)
    c: Horizontal(g68)
    c: Horizontal(g70)
    c: Vertical(g69)
    c: Vertical(g71)
    c: Coincident(g72,g73)
    c: Coincident(g73,g74)
    c: Coincident(g74,g75)
    c: Coincident(g75,g72)
    c: Horizontal(g72)
    c: Horizontal(g74)
    c: Vertical(g73)
    c: Vertical(g75)
    c: DistanceX(g4,g4) = 8
    c: Equal(g70,g66)
    c: Equal(g66,g74)
    c: Equal(g74,g6)
    c: Equal(g6,g8)
    c: Equal(g8,g16)
    c: Equal(g16,g14)
    c: Equal(g14,g22)
    c: Equal(g22,g24)
    c: Equal(g24,g28)
    c: Equal(g28,g32)
    c: Equal(g32,g36)
    c: Equal(g36,g40)
    c: Equal(g40,g46)
    c: Equal(g46,g54)
    c: Equal(g54,g58)
    c: Equal(g58,g62)
    c: DistanceY(g5,g5) = 30
    c: Equal(g5,g9)
    c: Equal(g9,g13)
    c: Equal(g13,g17)
    c: Equal(g17,g21)
    c: Equal(g21,g25)
    c: Equal(g25,g29)
    c: Equal(g29,g33)
    c: Equal(g33,g37)
    c: Equal(g37,g41)
    c: Equal(g41,g45)
    c: Equal(g45,g49)
    c: Equal(g49,g53)
    c: Equal(g53,g57)
    c: Equal(g57,g61)
    c: Equal(g61,g65)
    c: Equal(g65,g69)
    c: Equal(g69,g73)
    c: Coincident(g1,g85)
    c: Coincident(g42,g85)
    c: Coincident(g40,g84)
    c: Coincident(g46,g84)
    c: Coincident(g44,g83)
    c: Coincident(g50,g83)
    c: Coincident(g48,g82)
    c: Coincident(g54,g82)
    c: Coincident(g52,g81)
    c: Coincident(g58,g81)
    c: Coincident(g56,g80)
    c: Coincident(g62,g80)
    c: Coincident(g60,g79)
    c: Coincident(g66,g79)
    c: Coincident(g64,g78)
    c: Coincident(g70,g78)
    c: Coincident(g68,g77)
    c: Coincident(g74,g77)
    c: Coincident(g72,g76)
    c: Coincident(g0,g76)
    c: Equal(g76,g77)
    c: Equal(g77,g78)
    c: Equal(g78,g79)
    c: Equal(g79,g80)
    c: Equal(g80,g81)
    c: Equal(g81,g82)
    c: Equal(g82,g83)
    c: Equal(g83,g84)
    c: Equal(g84,g85)
    c: Vertical(g85)
    c: Vertical(g84)
    c: Vertical(g83)
    c: Vertical(g82)
    c: Vertical(g81)
    c: Vertical(g80)
    c: Vertical(g78)
    c: Vertical(g77)
    c: Vertical(g76)
    c: Coincident(g86,g0)
    c: Coincident(g4,g86)
    c: Coincident(g2,g95)
    c: Coincident(g38,g95)
    c: Coincident(g36,g94)
    c: Coincident(g34,g94)
    c: Coincident(g32,g93)
    c: Coincident(g30,g93)
    c: Coincident(g26,g92)
    c: Coincident(g28,g92)
    c: Coincident(g24,g91)
    c: Coincident(g22,g91)
    c: Coincident(g20,g90)
    c: Coincident(g18,g90)
    c: Coincident(g16,g89)
    c: Coincident(g14,g89)
    c: Coincident(g12,g88)
    c: Coincident(g10,g88)
    c: Coincident(g8,g87)
    c: Coincident(g6,g87)
    c: Equal(g87,g86)
    c: Equal(g86,g88)
    c: Equal(g88,g89)
    c: Equal(g89,g90)
    c: Equal(g90,g91)
    c: Equal(g91,g92)
    c: Equal(g92,g93)
    c: Equal(g93,g94)
    c: Equal(g94,g95)
    c: Vertical(g95)
    c: Vertical(g94)
    c: Vertical(g93)
    c: Vertical(g92)
    c: Vertical(g91)
    c: Vertical(g90)
    c: Vertical(g88)
    c: Vertical(g87)
    c: Vertical(g86)
    c: Symmetric(g0,g2,g-1)
    c: Equal(g50,g44)
    c: Tangent(g96,g99) = 1.5708
    c: Tangent(g96,g98) = -1.5708
    c: Tangent(g98,g97) = -1.5708
    c: Tangent(g99,g97) = 1.5708
    c: Equal(g96,g97)
    c: Symmetric(g96,g97,g-2)
    c: Radius(g97) = 15
    c: DistanceX(g99,g99) = 50
    c: DistanceY(g97,g0) = 40
    c: Coincident(g100,g101)
    c: Coincident(g101,g102)
    c: Coincident(g102,g103)
    c: Coincident(g103,g100)
    c: Horizontal(g100)
    c: Horizontal(g102)
    c: Vertical(g101)
    c: Vertical(g103)
    c: Coincident(g104,g105)
    c: Coincident(g105,g106)
    c: Coincident(g106,g107)
    c: Coincident(g107,g104)
    c: Horizontal(g104)
    c: Horizontal(g106)
    c: Vertical(g105)
    c: Vertical(g107)
    c: Coincident(g108,g109)
    c: Coincident(g109,g110)
    c: Coincident(g110,g111)
    c: Coincident(g111,g108)
    c: Horizontal(g108)
    c: Horizontal(g110)
    c: Vertical(g109)
    c: Vertical(g111)
    c: Coincident(g112,g113)
    c: Coincident(g113,g114)
    c: Coincident(g114,g115)
    c: Coincident(g115,g112)
    c: Horizontal(g112)
    c: Horizontal(g114)
    c: Vertical(g113)
    c: Vertical(g115)
    c: PointOnObject(g120,g69)
    c: Coincident(g113,g120)
    c: Coincident(g114,g119)
    c: Coincident(g109,g119)
    c: Coincident(g110,g118)
    c: Coincident(g105,g118)
    c: Coincident(g106,g117)
    c: Coincident(g101,g117)
    c: Coincident(g102,g116)
    c: PointOnObject(g116,g9)
    c: Equal(g118,g119)
    c: Equal(g119,g120)
    c: Equal(g120,g116)
    c: Equal(g116,g117)
    c: Equal(g101,g107)
    c: Equal(g107,g111)
    c: Equal(g111,g115)
    c: DistanceY(g103,g103) = 8
    c: Horizontal(g116)
    c: Horizontal(g117)
    c: Horizontal(g118)
    c: Horizontal(g119)
    c: Horizontal(g120)
    c: Equal(g100,g104)
    c: Equal(g104,g108)
    c: Equal(g108,g112)
    c: DistanceX(g100,g100) = 30
    c: DistanceY(g116,g0) = 88
    c: Coincident(g121,g122)
    c: Coincident(g122,g123)
    c: Coincident(g123,g124)
    c: Coincident(g124,g121)
    c: Horizontal(g121)
    c: Horizontal(g123)
    c: Vertical(g122)
    c: Vertical(g124)
    c: Coincident(g125,g126)
    c: Coincident(g126,g127)
    c: Coincident(g127,g128)
    c: Coincident(g128,g125)
    c: Horizontal(g125)
    c: Horizontal(g127)
    c: Vertical(g126)
    c: Vertical(g128)
    c: Coincident(g129,g130)
    c: Coincident(g130,g131)
    c: Coincident(g131,g132)
    c: Coincident(g132,g129)
    c: Horizontal(g129)
    c: Horizontal(g131)
    c: Vertical(g130)
    c: Vertical(g132)
    c: Coincident(g133,g134)
    c: Coincident(g134,g135)
    c: Coincident(g135,g136)
    c: Coincident(g136,g133)
    c: Horizontal(g133)
    c: Horizontal(g135)
    c: Vertical(g134)
    c: Vertical(g136)
    c: Coincident(g134,g141)
    c: Coincident(g135,g139)
    c: Coincident(g130,g139)
    c: Coincident(g131,g138)
    c: Coincident(g126,g138)
    c: Coincident(g127,g137)
    c: Coincident(g122,g137)
    c: Coincident(g123,g140)
    c: Equal(g138,g139)
    c: Equal(g139,g141)
    c: Equal(g141,g140)
    c: Equal(g140,g137)
    c: Equal(g122,g128)
    c: Equal(g128,g132)
    c: Equal(g132,g136)
    c: Equal(g103,g124) = 8
    c: Horizontal(g140)
    c: Horizontal(g137)
    c: Horizontal(g138)
    c: Horizontal(g139)
    c: Horizontal(g141)
    c: Equal(g121,g125)
    c: Equal(g125,g129)
    c: Equal(g129,g133)
    c: Equal(g100,g121) = 30
    c: PointOnObject(g141,g41)
    c: PointOnObject(g140,g37)
    c: DistanceY(g2,g141) = 10
    c: DistanceY(g121,g142) = 5
    c: DistanceX(g37,g142) = 10
    c: Radius(g142) = 1.55
    c: DistanceY(g133,g143) = 5
    c: DistanceX(g143,g41) = 10
    c: Radius(g143) = 1.55
    c: DistanceX(g21,g144) = 10
    c: DistanceY(g21,g144) = 5
    c: Radius(g144) = 1.55
    c: DistanceX(g145,g57) = 10
    c: DistanceY(g57,g145) = 5
    c: Radius(g145) = 1.55
    c: DistanceY(g100,g146) = 5
    c: DistanceX(g5,g146) = 10
    c: Radius(g146) = 1.55
    c: DistanceY(g112,g147) = 5
    c: DistanceX(g147,g73) = 10
    c: Radius(g147) = 1.55
FEATURE [Sketcher::SketchObject] Sketch005  label="back"
  sketch-geometry (182):
    g0: LineSegment StartX=-202.5 StartY=329 StartZ=0 EndX=202.5 EndY=329 EndZ=0
    g1: LineSegment [constr] StartX=202.5 StartY=329 StartZ=0 EndX=202.5 EndY=-329 EndZ=0
    g2: LineSegment StartX=202.5 StartY=-329 StartZ=0 EndX=-202.5 EndY=-329 EndZ=0
    g3: LineSegment [constr] StartX=-202.5 StartY=-329 StartZ=0 EndX=-202.5 EndY=329 EndZ=0
    g4: LineSegment [constr] StartX=-202.5 StartY=-319 StartZ=0 EndX=202.5 EndY=-319 EndZ=0
    g5: LineSegment StartX=-145.5 StartY=-319 StartZ=0 EndX=-115.5 EndY=-319 EndZ=0
    g6: LineSegment StartX=-115.5 StartY=-319 StartZ=0 EndX=-115.5 EndY=-311 EndZ=0
    g7: LineSegment StartX=-115.5 StartY=-311 StartZ=0 EndX=-145.5 EndY=-311 EndZ=0
    g8: LineSegment StartX=-145.5 StartY=-311 StartZ=0 EndX=-145.5 EndY=-319 EndZ=0
    g9: LineSegment StartX=-58.5 StartY=-319 StartZ=0 EndX=-28.5 EndY=-319 EndZ=0
    g10: LineSegment StartX=-28.5 StartY=-319 StartZ=0 EndX=-28.5 EndY=-311 EndZ=0
    g11: LineSegment StartX=-28.5 StartY=-311 StartZ=0 EndX=-58.5 EndY=-311 EndZ=0
    g12: LineSegment StartX=-58.5 StartY=-311 StartZ=0 EndX=-58.5 EndY=-319 EndZ=0
    g13: LineSegment StartX=28.5 StartY=-319 StartZ=0 EndX=58.5 EndY=-319 EndZ=0
    g14: LineSegment StartX=58.5 StartY=-319 StartZ=0 EndX=58.5 EndY=-311 EndZ=0
    g15: LineSegment StartX=58.5 StartY=-311 StartZ=0 EndX=28.5 EndY=-311 EndZ=0
    g16: LineSegment StartX=28.5 StartY=-311 StartZ=0 EndX=28.5 EndY=-319 EndZ=0
    g17: LineSegment StartX=115.5 StartY=-319 StartZ=0 EndX=145.5 EndY=-319 EndZ=0
    g18: LineSegment StartX=145.5 StartY=-319 StartZ=0 EndX=145.5 EndY=-311 EndZ=0
    g19: LineSegment StartX=145.5 StartY=-311 StartZ=0 EndX=115.5 EndY=-311 EndZ=0
    g20: LineSegment StartX=115.5 StartY=-311 StartZ=0 EndX=115.5 EndY=-319 EndZ=0
    g21: LineSegment [constr] StartX=-202.5 StartY=-319 StartZ=0 EndX=-145.5 EndY=-319 EndZ=0
    g22: LineSegment [constr] StartX=-115.5 StartY=-319 StartZ=0 EndX=-58.5 EndY=-319 EndZ=0
    g23: LineSegment [constr] StartX=-28.5 StartY=-319 StartZ=0 EndX=28.5 EndY=-319 EndZ=0
    g24: LineSegment [constr] StartX=58.5 StartY=-319 StartZ=0 EndX=115.5 EndY=-319 EndZ=0
    g25: LineSegment [constr] StartX=145.5 StartY=-319 StartZ=0 EndX=202.5 EndY=-319 EndZ=0
    g26: LineSegment [constr] StartX=-15 StartY=-275 StartZ=0 EndX=15 EndY=-275 EndZ=0
    g27: LineSegment [constr] StartX=15 StartY=-275 StartZ=0 EndX=15 EndY=-305 EndZ=0
    g28: LineSegment [constr] StartX=15 StartY=-305 StartZ=0 EndX=-15 EndY=-305 EndZ=0
    g29: LineSegment [constr] StartX=-15 StartY=-305 StartZ=0 EndX=-15 EndY=-275 EndZ=0
    g30: Circle CenterX=-15 CenterY=-305 CenterZ=0 NormalX=0 NormalY=0 NormalZ=1 AngleXU=0 Radius=2.1
    g31: Circle CenterX=15 CenterY=-305 CenterZ=0 NormalX=0 NormalY=0 NormalZ=1 AngleXU=0 Radius=2.1
    g32: Circle CenterX=15 CenterY=-275 CenterZ=0 NormalX=0 NormalY=0 NormalZ=1 AngleXU=0 Radius=2.1
    g33: Circle CenterX=-15 CenterY=-275 CenterZ=0 NormalX=0 NormalY=0 NormalZ=1 AngleXU=0 Radius=2.1
    g34: LineSegment [constr] StartX=-202.5 StartY=241 StartZ=0 EndX=202.5 EndY=241 EndZ=0
    g35: LineSegment StartX=-145.5 StartY=241 StartZ=0 EndX=-115.5 EndY=241 EndZ=0
    g36: LineSegment StartX=-115.5 StartY=241 StartZ=0 EndX=-115.5 EndY=249 EndZ=0
    g37: LineSegment StartX=-115.5 StartY=249 StartZ=0 EndX=-145.5 EndY=249 EndZ=0
    g38: LineSegment StartX=-145.5 StartY=249 StartZ=0 EndX=-145.5 EndY=241 EndZ=0
    g39: LineSegment StartX=-58.5 StartY=241 StartZ=0 EndX=-28.5 EndY=241 EndZ=0
    g40: LineSegment StartX=-28.5 StartY=241 StartZ=0 EndX=-28.5 EndY=249 EndZ=0
    g41: LineSegment StartX=-28.5 StartY=249 StartZ=0 EndX=-58.5 EndY=249 EndZ=0
    g42: LineSegment StartX=-58.5 StartY=249 StartZ=0 EndX=-58.5 EndY=241 EndZ=0
    g43: LineSegment StartX=28.5 StartY=241 StartZ=0 EndX=58.5 EndY=241 EndZ=0
    g44: LineSegment StartX=58.5 StartY=241 StartZ=0 EndX=58.5 EndY=249 EndZ=0
    g45: LineSegment StartX=58.5 StartY=249 StartZ=0 EndX=28.5 EndY=249 EndZ=0
    g46: LineSegment StartX=28.5 StartY=249 StartZ=0 EndX=28.5 EndY=241 EndZ=0
    g47: LineSegment StartX=115.5 StartY=241 StartZ=0 EndX=145.5 EndY=241 EndZ=0
    g48: LineSegment StartX=145.5 StartY=241 StartZ=0 EndX=145.5 EndY=249 EndZ=0
    g49: LineSegment StartX=145.5 StartY=249 StartZ=0 EndX=115.5 EndY=249 EndZ=0
    g50: LineSegment StartX=115.5 StartY=249 StartZ=0 EndX=115.5 EndY=241 EndZ=0
    g51: LineSegment [constr] StartX=-202.5 StartY=241 StartZ=0 EndX=-145.5 EndY=241 EndZ=0
    g52: LineSegment [constr] StartX=-115.5 StartY=241 StartZ=0 EndX=-58.5 EndY=241 EndZ=0
    g53: LineSegment [constr] StartX=-28.5 StartY=241 StartZ=0 EndX=28.5 EndY=241 EndZ=0
    g54: LineSegment [constr] StartX=58.5 StartY=241 StartZ=0 EndX=115.5 EndY=241 EndZ=0
    g55: LineSegment [constr] StartX=145.5 StartY=241 StartZ=0 EndX=202.5 EndY=241 EndZ=0
    g56: LineSegment [constr] StartX=-15 StartY=285 StartZ=0 EndX=15 EndY=285 EndZ=0
    g57: LineSegment [constr] StartX=15 StartY=285 StartZ=0 EndX=15 EndY=255 EndZ=0
    g58: LineSegment [constr] StartX=15 StartY=255 StartZ=0 EndX=-15 EndY=255 EndZ=0
    g59: LineSegment [constr] StartX=-15 StartY=255 StartZ=0 EndX=-15 EndY=285 EndZ=0
    g60: Circle CenterX=-15 CenterY=255 CenterZ=0 NormalX=0 NormalY=0 NormalZ=1 AngleXU=0 Radius=2.1
    g61: Circle CenterX=15 CenterY=255 CenterZ=0 NormalX=0 NormalY=0 NormalZ=1 AngleXU=0 Radius=2.1
    g62: Circle CenterX=15 CenterY=285 CenterZ=0 NormalX=0 NormalY=0 NormalZ=1 AngleXU=0 Radius=2.1
    g63: Circle CenterX=-15 CenterY=285 CenterZ=0 NormalX=0 NormalY=0 NormalZ=1 AngleXU=0 Radius=2.1
    g64: LineSegment [constr] StartX=-145.5 StartY=319.75 StartZ=0 EndX=-84 EndY=319.75 EndZ=0
    g65: LineSegment [constr] StartX=-84 StartY=319.75 StartZ=0 EndX=-84 EndY=258.25 EndZ=0
    g66: LineSegment [constr] StartX=-84 StartY=258.25 StartZ=0 EndX=-145.5 EndY=258.25 EndZ=0
    g67: LineSegment [constr] StartX=-145.5 StartY=258.25 StartZ=0 EndX=-145.5 EndY=319.75 EndZ=0
    g68: Circle CenterX=-145.5 CenterY=258.25 CenterZ=0 NormalX=0 NormalY=0 NormalZ=1 AngleXU=0 Radius=1.55
    g69: Circle CenterX=-84 CenterY=258.25 CenterZ=0 NormalX=0 NormalY=0 NormalZ=1 AngleXU=0 Radius=1.55
    g70: Circle CenterX=-145.5 CenterY=319.75 CenterZ=0 NormalX=0 NormalY=0 NormalZ=1 AngleXU=0 Radius=1.55
    g71: Circle CenterX=-84 CenterY=319.75 CenterZ=0 NormalX=0 NormalY=0 NormalZ=1 AngleXU=0 Radius=1.55
    g72: LineSegment [constr] StartX=-145.5 StartY=249 StartZ=0 EndX=-145.5 EndY=258.25 EndZ=0
    g73: LineSegment [constr] StartX=-145.5 StartY=319.75 StartZ=0 EndX=-145.5 EndY=329 EndZ=0
    g74: Circle CenterX=-114.75 CenterY=289 CenterZ=0 NormalX=0 NormalY=0 NormalZ=1 AngleXU=0 Radius=35
    g75: LineSegment [constr] StartX=115.5 StartY=249 StartZ=0 EndX=115.5 EndY=275 EndZ=0
    g76: LineSegment [constr] StartX=115.5 StartY=329 StartZ=0 EndX=115.5 EndY=303 EndZ=0
    g77: LineSegment StartX=115.5 StartY=303 StartZ=0 EndX=163.5 EndY=303 EndZ=0
    g78: LineSegment StartX=163.5 StartY=303 StartZ=0 EndX=163.5 EndY=275 EndZ=0
    g79: LineSegment StartX=163.5 StartY=275 StartZ=0 EndX=115.5 EndY=275 EndZ=0
    g80: LineSegment StartX=115.5 StartY=275 StartZ=0 EndX=115.5 EndY=303 EndZ=0
    g81: LineSegment [constr] StartX=139.5 StartY=269 StartZ=0 EndX=139.5 EndY=309 EndZ=0
    g82: Circle CenterX=139.5 CenterY=269 CenterZ=0 NormalX=0 NormalY=0 NormalZ=1 AngleXU=0 Radius=2
    g83: Circle CenterX=139.5 CenterY=309 CenterZ=0 NormalX=0 NormalY=0 NormalZ=1 AngleXU=0 Radius=2
    g84: LineSegment StartX=-210.5 StartY=290.2 StartZ=0 EndX=-202.5 EndY=290.2 EndZ=0
    g85: LineSegment [constr] StartX=-202.5 StartY=290.2 StartZ=0 EndX=-202.5 EndY=260.2 EndZ=0
    g86: LineSegment StartX=-202.5 StartY=260.2 StartZ=0 EndX=-210.5 EndY=260.2 EndZ=0
    g87: LineSegment StartX=-210.5 StartY=260.2 StartZ=0 EndX=-210.5 EndY=290.2 EndZ=0
    g88: LineSegment StartX=-210.5 StartY=221.4 StartZ=0 EndX=-202.5 EndY=221.4 EndZ=0
    g89: LineSegment [constr] StartX=-202.5 StartY=221.4 StartZ=0 EndX=-202.5 EndY=191.4 EndZ=0
    g90: LineSegment StartX=-202.5 StartY=191.4 StartZ=0 EndX=-210.5 EndY=191.4 EndZ=0
    g91: LineSegment StartX=-210.5 StartY=191.4 StartZ=0 EndX=-210.5 EndY=221.4 EndZ=0
    g92: LineSegment StartX=-210.5 StartY=152.6 StartZ=0 EndX=-202.5 EndY=152.6 EndZ=0
    g93: LineSegment [constr] StartX=-202.5 StartY=152.6 StartZ=0 EndX=-202.5 EndY=122.6 EndZ=0
    g94: LineSegment StartX=-202.5 StartY=122.6 StartZ=0 EndX=-210.5 EndY=122.6 EndZ=0
    g95: LineSegment StartX=-210.5 StartY=122.6 StartZ=0 EndX=-210.5 EndY=152.6 EndZ=0
    g96: LineSegment StartX=-210.5 StartY=83.8 StartZ=0 EndX=-202.5 EndY=83.8 EndZ=0
    g97: LineSegment [constr] StartX=-202.5 StartY=83.8 StartZ=0 EndX=-202.5 EndY=53.8 EndZ=0
    g98: LineSegment StartX=-202.5 StartY=53.8 StartZ=0 EndX=-210.5 EndY=53.8 EndZ=0
    g99: LineSegment StartX=-210.5 StartY=53.8 StartZ=0 EndX=-210.5 EndY=83.8 EndZ=0
    g100: LineSegment StartX=-210.5 StartY=15 StartZ=0 EndX=-202.5 EndY=15 EndZ=0
    g101: LineSegment [constr] StartX=-202.5 StartY=15 StartZ=0 EndX=-202.5 EndY=-15 EndZ=0
    g102: LineSegment StartX=-202.5 StartY=-15 StartZ=0 EndX=-210.5 EndY=-15 EndZ=0
    g103: LineSegment StartX=-210.5 StartY=-15 StartZ=0 EndX=-210.5 EndY=15 EndZ=0
    g104: LineSegment StartX=-210.5 StartY=-53.8 StartZ=0 EndX=-202.5 EndY=-53.8 EndZ=0
    g105: LineSegment [constr] StartX=-202.5 StartY=-53.8 StartZ=0 EndX=-202.5 EndY=-83.8 EndZ=0
    g106: LineSegment StartX=-202.5 StartY=-83.8 StartZ=0 EndX=-210.5 EndY=-83.8 EndZ=0
    g107: LineSegment StartX=-210.5 StartY=-83.8 StartZ=0 EndX=-210.5 EndY=-53.8 EndZ=0
    g108: LineSegment StartX=-210.5 StartY=-122.6 StartZ=0 EndX=-202.5 EndY=-122.6 EndZ=0
    g109: LineSegment [constr] StartX=-202.5 StartY=-122.6 StartZ=0 EndX=-202.5 EndY=-152.6 EndZ=0
    g110: LineSegment StartX=-202.5 StartY=-152.6 StartZ=0 EndX=-210.5 EndY=-152.6 EndZ=0
    g111: LineSegment StartX=-210.5 StartY=-152.6 StartZ=0 EndX=-210.5 EndY=-122.6 EndZ=0
    g112: LineSegment StartX=-210.5 StartY=-191.4 StartZ=0 EndX=-202.5 EndY=-191.4 EndZ=0
    g113: LineSegment [constr] StartX=-202.5 StartY=-191.4 StartZ=0 EndX=-202.5 EndY=-221.4 EndZ=0
    g114: LineSegment StartX=-202.5 StartY=-221.4 StartZ=0 EndX=-210.5 EndY=-221.4 EndZ=0
    g115: LineSegment StartX=-210.5 StartY=-221.4 StartZ=0 EndX=-210.5 EndY=-191.4 EndZ=0
    g116: LineSegment StartX=-210.5 StartY=-260.2 StartZ=0 EndX=-202.5 EndY=-260.2 EndZ=0
    g117: LineSegment [constr] StartX=-202.5 StartY=-260.2 StartZ=0 EndX=-202.5 EndY=-290.2 EndZ=0
    g118: LineSegment StartX=-202.5 StartY=-290.2 StartZ=0 EndX=-210.5 EndY=-290.2 EndZ=0
    g119: LineSegment StartX=-210.5 StartY=-290.2 StartZ=0 EndX=-210.5 EndY=-260.2 EndZ=0
    g120: LineSegment StartX=-202.5 StartY=260.2 StartZ=0 EndX=-202.5 EndY=221.4 EndZ=0
    g121: LineSegment StartX=-202.5 StartY=191.4 StartZ=0 EndX=-202.5 EndY=152.6 EndZ=0
    g122: LineSegment StartX=-202.5 StartY=122.6 StartZ=0 EndX=-202.5 EndY=83.8 EndZ=0
    g123: LineSegment StartX=-202.5 StartY=15 StartZ=0 EndX=-202.5 EndY=53.8 EndZ=0
    g124: LineSegment StartX=-202.5 StartY=-53.8 StartZ=0 EndX=-202.5 EndY=-15 EndZ=0
    g125: LineSegment StartX=-202.5 StartY=-122.6 StartZ=0 EndX=-202.5 EndY=-83.8 EndZ=0
    g126: LineSegment StartX=-202.5 StartY=-191.4 StartZ=0 EndX=-202.5 EndY=-152.6 EndZ=0
    g127: LineSegment StartX=-202.5 StartY=-260.2 StartZ=0 EndX=-202.5 EndY=-221.4 EndZ=0
    g128: LineSegment StartX=-202.5 StartY=-329 StartZ=0 EndX=-202.5 EndY=-290.2 EndZ=0
    g129: LineSegment StartX=-202.5 StartY=329 StartZ=0 EndX=-202.5 EndY=290.2 EndZ=0
    g130: LineSegment StartX=202.5 StartY=-260.2 StartZ=0 EndX=210.5 EndY=-260.2 EndZ=0
    g131: LineSegment StartX=210.5 StartY=-260.2 StartZ=0 EndX=210.5 EndY=-290.2 EndZ=0
    g132: LineSegment StartX=210.5 StartY=-290.2 StartZ=0 EndX=202.5 EndY=-290.2 EndZ=0
    g133: LineSegment [constr] StartX=202.5 StartY=-290.2 StartZ=0 EndX=202.5 EndY=-260.2 EndZ=0
    g134: LineSegment StartX=202.5 StartY=-191.4 StartZ=0 EndX=210.5 EndY=-191.4 EndZ=0
    g135: LineSegment StartX=210.5 StartY=-191.4 StartZ=0 EndX=210.5 EndY=-221.4 EndZ=0
    g136: LineSegment StartX=210.5 StartY=-221.4 StartZ=0 EndX=202.5 EndY=-221.4 EndZ=0
    g137: LineSegment [constr] StartX=202.5 StartY=-221.4 StartZ=0 EndX=202.5 EndY=-191.4 EndZ=0
    g138: LineSegment StartX=202.5 StartY=-122.6 StartZ=0 EndX=210.5 EndY=-122.6 EndZ=0
    g139: LineSegment StartX=210.5 StartY=-122.6 StartZ=0 EndX=210.5 EndY=-152.6 EndZ=0
    g140: LineSegment StartX=210.5 StartY=-152.6 StartZ=0 EndX=202.5 EndY=-152.6 EndZ=0
    g141: LineSegment [constr] StartX=202.5 StartY=-152.6 StartZ=0 EndX=202.5 EndY=-122.6 EndZ=0
    g142: LineSegment StartX=202.5 StartY=-53.8 StartZ=0 EndX=210.5 EndY=-53.8 EndZ=0
    g143: LineSegment StartX=210.5 StartY=-53.8 StartZ=0 EndX=210.5 EndY=-83.8 EndZ=0
    g144: LineSegment StartX=210.5 StartY=-83.8 StartZ=0 EndX=202.5 EndY=-83.8 EndZ=0
    g145: LineSegment [constr] StartX=202.5 StartY=-83.8 StartZ=0 EndX=202.5 EndY=-53.8 EndZ=0
    g146: LineSegment StartX=202.5 StartY=15 StartZ=0 EndX=210.5 EndY=15 EndZ=0
    g147: LineSegment StartX=210.5 StartY=15 StartZ=0 EndX=210.5 EndY=-15 EndZ=0
    g148: LineSegment StartX=210.5 StartY=-15 StartZ=0 EndX=202.5 EndY=-15 EndZ=0
    g149: LineSegment [constr] StartX=202.5 StartY=-15 StartZ=0 EndX=202.5 EndY=15 EndZ=0
    g150: LineSegment StartX=202.5 StartY=83.8 StartZ=0 EndX=210.5 EndY=83.8 EndZ=0
    g151: LineSegment StartX=210.5 StartY=83.8 StartZ=0 EndX=210.5 EndY=53.8 EndZ=0
    g152: LineSegment StartX=210.5 StartY=53.8 StartZ=0 EndX=202.5 EndY=53.8 EndZ=0
    g153: LineSegment [constr] StartX=202.5 StartY=53.8 StartZ=0 EndX=202.5 EndY=83.8 EndZ=0
    g154: LineSegment StartX=202.5 StartY=152.6 StartZ=0 EndX=210.5 EndY=152.6 EndZ=0
    g155: LineSegment StartX=210.5 StartY=152.6 StartZ=0 EndX=210.5 EndY=122.6 EndZ=0
    g156: LineSegment StartX=210.5 StartY=122.6 StartZ=0 EndX=202.5 EndY=122.6 EndZ=0
    g157: LineSegment [constr] StartX=202.5 StartY=122.6 StartZ=0 EndX=202.5 EndY=152.6 EndZ=0
    g158: LineSegment StartX=202.5 StartY=221.4 StartZ=0 EndX=210.5 EndY=221.4 EndZ=0
    g159: LineSegment StartX=210.5 StartY=221.4 StartZ=0 EndX=210.5 EndY=191.4 EndZ=0
    g160: LineSegment StartX=210.5 StartY=191.4 StartZ=0 EndX=202.5 EndY=191.4 EndZ=0
    g161: LineSegment [constr] StartX=202.5 StartY=191.4 StartZ=0 EndX=202.5 EndY=221.4 EndZ=0
    g162: LineSegment StartX=202.5 StartY=290.2 StartZ=0 EndX=210.5 EndY=290.2 EndZ=0
    g163: LineSegment StartX=210.5 StartY=290.2 StartZ=0 EndX=210.5 EndY=260.2 EndZ=0
    g164: LineSegment StartX=210.5 StartY=260.2 StartZ=0 EndX=202.5 EndY=260.2 EndZ=0
    g165: LineSegment [constr] StartX=202.5 StartY=260.2 StartZ=0 EndX=202.5 EndY=290.2 EndZ=0
    g166: LineSegment StartX=202.5 StartY=260.2 StartZ=0 EndX=202.5 EndY=221.4 EndZ=0
    g167: LineSegment StartX=202.5 StartY=191.4 StartZ=0 EndX=202.5 EndY=152.6 EndZ=0
    g168: LineSegment StartX=202.5 StartY=83.8 StartZ=0 EndX=202.5 EndY=122.6 EndZ=0
    g169: LineSegment StartX=202.5 StartY=15 StartZ=0 EndX=202.5 EndY=53.8 EndZ=0
    g170: LineSegment StartX=202.5 StartY=-53.8 StartZ=0 EndX=202.5 EndY=-15 EndZ=0
    g171: LineSegment StartX=202.5 StartY=-122.6 StartZ=0 EndX=202.5 EndY=-83.8 EndZ=0
    g172: LineSegment StartX=202.5 StartY=-191.4 StartZ=0 EndX=202.5 EndY=-152.6 EndZ=0
    g173: LineSegment StartX=202.5 StartY=-260.2 StartZ=0 EndX=202.5 EndY=-221.4 EndZ=0
    g174: LineSegment StartX=202.5 StartY=290.2 StartZ=0 EndX=202.5 EndY=329 EndZ=0
    g175: LineSegment StartX=202.5 StartY=-290.2 StartZ=0 EndX=202.5 EndY=-329 EndZ=0
    g176: Circle CenterX=192.5 CenterY=254 CenterZ=0 NormalX=0 NormalY=0 NormalZ=1 AngleXU=0 Radius=1.55
    g177: Circle CenterX=-192.5 CenterY=254 CenterZ=0 NormalX=0 NormalY=0 NormalZ=1 AngleXU=0 Radius=1.55
    g178: Circle CenterX=-192.5 CenterY=-306 CenterZ=0 NormalX=0 NormalY=0 NormalZ=1 AngleXU=0 Radius=1.55
    g179: Circle CenterX=192.5 CenterY=-306 CenterZ=0 NormalX=0 NormalY=0 NormalZ=1 AngleXU=0 Radius=1.55
    g180: Circle CenterX=-192.5 CenterY=-10 CenterZ=0 NormalX=0 NormalY=0 NormalZ=1 AngleXU=0 Radius=1.55
    g181: Circle CenterX=192.5 CenterY=-10 CenterZ=0 NormalX=0 NormalY=0 NormalZ=1 AngleXU=0 Radius=1.55
  constraints (498):
    c: Coincident(g0,g1)
    c: Coincident(g1,g2)
    c: Coincident(g2,g3)
    c: Coincident(g3,g0)
    c: Vertical(g1)
    c: DistanceX(g2,g2) = 405
    c: PointOnObject(g4,g1)
    c: Coincident(g5,g6)
    c: Coincident(g6,g7)
    c: Coincident(g7,g8)
    c: Coincident(g8,g5)
    c: Horizontal(g5)
    c: Horizontal(g7)
    c: Vertical(g6)
    c: Vertical(g8)
    c: Coincident(g9,g10)
    c: Coincident(g10,g11)
    c: Coincident(g11,g12)
    c: Coincident(g12,g9)
    c: Horizontal(g9)
    c: Horizontal(g11)
    c: Vertical(g10)
    c: Vertical(g12)
    c: Coincident(g13,g14)
    c: Coincident(g14,g15)
    c: Coincident(g15,g16)
    c: Coincident(g16,g13)
    c: Horizontal(g13)
    c: Horizontal(g15)
    c: Vertical(g14)
    c: Vertical(g16)
    c: Coincident(g17,g18)
    c: Coincident(g18,g19)
    c: Coincident(g19,g20)
    c: Coincident(g20,g17)
    c: Horizontal(g17)
    c: Horizontal(g19)
    c: Vertical(g18)
    c: Vertical(g20)
    c: Equal(g17,g13)
    c: Equal(g13,g9)
    c: Equal(g9,g5)
    c: DistanceX(g7,g7) = 30
    c: PointOnObject(g5,g4)
    c: PointOnObject(g9,g4)
    c: PointOnObject(g13,g4)
    c: PointOnObject(g17,g4)
    c: Equal(g20,g14)
    c: Equal(g14,g12)
    c: Equal(g12,g6)
    c: DistanceY(g8,g8) = 8
    c: Equal(g25,g24)
    c: Equal(g24,g23)
    c: Equal(g23,g22)
    c: Equal(g22,g21)
    c: Coincident(g4,g25)
    c: Coincident(g17,g25)
    c: Coincident(g17,g24)
    c: Coincident(g13,g24)
    c: Coincident(g13,g23)
    c: Coincident(g9,g23)
    c: Coincident(g22,g9)
    c: Coincident(g5,g22)
    c: Coincident(g5,g21)
    c: Coincident(g4,g21)
    c: Coincident(g26,g27)
    c: Coincident(g27,g28)
    c: Coincident(g28,g29)
    c: Coincident(g29,g26)
    c: Horizontal(g26)
    c: Vertical(g27)
    c: Vertical(g29)
    c: Symmetric(g27,g28,g-2)
    c: Coincident(g26,g33)
    c: Coincident(g26,g32)
    c: Coincident(g27,g31)
    c: Coincident(g28,g30)
    c: Radius(g30) = 2.1
    c: Equal(g30,g33)
    c: Equal(g30,g32)
    c: Equal(g30,g31)
    c: DistanceY(g15,g31) = 6
    c: DistanceX(g26,g26) = 30
    c: DistanceY(g27,g27) = 30
    c: DistanceY(g3,g3) = 658
    c: Horizontal(g34)
    c: Coincident(g35,g36)
    c: Coincident(g36,g37)
    c: Coincident(g37,g38)
    c: Coincident(g38,g35)
    c: Horizontal(g35)
    c: Horizontal(g37)
    c: Vertical(g36)
    c: Vertical(g38)
    c: Coincident(g39,g40)
    c: Coincident(g40,g41)
    c: Coincident(g41,g42)
    c: Coincident(g42,g39)
    c: Horizontal(g39)
    c: Horizontal(g41)
    c: Vertical(g40)
    c: Vertical(g42)
    c: Coincident(g43,g44)
    c: Coincident(g44,g45)
    c: Coincident(g45,g46)
    c: Coincident(g46,g43)
    c: Horizontal(g43)
    c: Horizontal(g45)
    c: Vertical(g44)
    c: Vertical(g46)
    c: Coincident(g47,g48)
    c: Coincident(g48,g49)
    c: Coincident(g49,g50)
    c: Coincident(g50,g47)
    c: Horizontal(g47)
    c: Horizontal(g49)
    c: Vertical(g48)
    c: Vertical(g50)
    c: Equal(g47,g43)
    c: Equal(g43,g39)
    c: Equal(g39,g35)
    c: Equal(g7,g37) = 30
    c: PointOnObject(g35,g34)
    c: PointOnObject(g39,g34)
    c: PointOnObject(g43,g34)
    c: PointOnObject(g47,g34)
    c: Equal(g50,g44)
    c: Equal(g44,g42)
    c: Equal(g42,g36)
    c: Equal(g8,g38) = 8
    c: Equal(g55,g54)
    c: Equal(g54,g53)
    c: Equal(g53,g52)
    c: Equal(g52,g51)
    c: Coincident(g34,g55)
    c: Coincident(g47,g55)
    c: Coincident(g47,g54)
    c: Coincident(g43,g54)
    c: Coincident(g43,g53)
    c: Coincident(g39,g53)
    c: Coincident(g52,g39)
    c: Coincident(g35,g52)
    c: Coincident(g35,g51)
    c: Coincident(g34,g51)
    c: Coincident(g56,g57)
    c: Coincident(g57,g58)
    c: Coincident(g58,g59)
    c: Coincident(g59,g56)
    c: Horizontal(g56)
    c: Vertical(g57)
    c: Vertical(g59)
    c: Coincident(g56,g63)
    c: Coincident(g56,g62)
    c: Coincident(g57,g61)
    c: Coincident(g58,g60)
    c: Equal(g30,g60) = 2.1
    c: Equal(g60,g63)
    c: Equal(g60,g62)
    c: Equal(g60,g61)
    c: DistanceY(g45,g61) = 6
    c: Equal(g26,g56) = 30
    c: Equal(g27,g57) = 30
    c: PointOnObject(g34,g3)
    c: PointOnObject(g34,g1)
    c: Symmetric(g60,g61,g-2)
    c: DistanceY(g34,g0) = 88
    c: Coincident(g64,g65)
    c: Coincident(g65,g66)
    c: Coincident(g66,g67)
    c: Coincident(g67,g64)
    c: Horizontal(g64)
    c: Horizontal(g66)
    c: Vertical(g65)
    c: Vertical(g67)
    c: Equal(g64,g65)
    c: DistanceX(g64,g64) = 61.5
    c: Coincident(g64,g71)
    c: Coincident(g64,g70)
    c: Coincident(g66,g68)
    c: Coincident(g65,g69)
    c: Radius(g71) = 1.55
    c: Equal(g71,g70)
    c: Equal(g71,g68)
    c: Equal(g71,g69)
    c: PointOnObject(g73,g0)
    c: Vertical(g73)
    c: Coincident(g73,g70)
    c: Coincident(g37,g72)
    c: Coincident(g66,g72)
    c: Vertical(g72)
    c: Equal(g72,g73)
    c: Radius(g74) = 35
    c: DistanceX(g70,g74) = 30.75
    c: DistanceY(g68,g74) = 30.75
    c: Coincident(g49,g75)
    c: PointOnObject(g76,g0)
    c: Vertical(g76)
    c: Vertical(g75)
    c: Equal(g76,g75)
    c: Coincident(g77,g78)
    c: Coincident(g78,g79)
    c: Coincident(g79,g80)
    c: Coincident(g80,g77)
    c: Horizontal(g77)
    c: Horizontal(g79)
    c: Vertical(g78)
    c: Vertical(g80)
    c: DistanceX(g77,g77) = 48
    c: DistanceY(g80,g80) = 28
    c: Coincident(g75,g79)
    c: Coincident(g76,g77)
    c: Symmetric(g77,g77,g81)
    c: DistanceY(g81,g81) = 40
    c: DistanceY(g81,g78) = 6
    c: Coincident(g81,g82)
    c: Coincident(g81,g83)
    c: Radius(g83) = 2
    c: Equal(g83,g82)
    c: Coincident(g84,g85)
    c: Coincident(g85,g86)
    c: Coincident(g86,g87)
    c: Coincident(g87,g84)
    c: Horizontal(g84)
    c: Horizontal(g86)
    c: Vertical(g85)
    c: Vertical(g87)
    c: Coincident(g88,g89)
    c: Coincident(g89,g90)
    c: Coincident(g90,g91)
    c: Coincident(g91,g88)
    c: Horizontal(g88)
    c: Horizontal(g90)
    c: Vertical(g89)
    c: Vertical(g91)
    c: Coincident(g92,g93)
    c: Coincident(g93,g94)
    c: Coincident(g94,g95)
    c: Coincident(g95,g92)
    c: Horizontal(g92)
    c: Horizontal(g94)
    c: Vertical(g93)
    c: Vertical(g95)
    c: Coincident(g96,g97)
    c: Coincident(g97,g98)
    c: Coincident(g98,g99)
    c: Coincident(g99,g96)
    c: Horizontal(g96)
    c: Horizontal(g98)
    c: Vertical(g97)
    c: Vertical(g99)
    c: Coincident(g100,g101)
    c: Coincident(g101,g102)
    c: Coincident(g102,g103)
    c: Coincident(g103,g100)
    c: Horizontal(g100)
    c: Horizontal(g102)
    c: Vertical(g101)
    c: Vertical(g103)
    c: Coincident(g104,g105)
    c: Coincident(g105,g106)
    c: Coincident(g106,g107)
    c: Coincident(g107,g104)
    c: Horizontal(g104)
    c: Horizontal(g106)
    c: Vertical(g105)
    c: Vertical(g107)
    c: Coincident(g108,g109)
    c: Coincident(g109,g110)
    c: Coincident(g110,g111)
    c: Coincident(g111,g108)
    c: Horizontal(g108)
    c: Horizontal(g110)
    c: Vertical(g109)
    c: Vertical(g111)
    c: Coincident(g112,g113)
    c: Coincident(g113,g114)
    c: Coincident(g114,g115)
    c: Coincident(g115,g112)
    c: Horizontal(g112)
    c: Horizontal(g114)
    c: Vertical(g113)
    c: Vertical(g115)
    c: Coincident(g116,g117)
    c: Coincident(g117,g118)
    c: Coincident(g118,g119)
    c: Coincident(g119,g116)
    c: Horizontal(g116)
    c: Horizontal(g118)
    c: Vertical(g117)
    c: Vertical(g119)
    c: Equal(g118,g114)
    c: Equal(g114,g110)
    c: Equal(g110,g106)
    c: Equal(g106,g102)
    c: Equal(g102,g98)
    c: Equal(g98,g94)
    c: Equal(g94,g90)
    c: Equal(g90,g86)
    c: DistanceX(g84,g84) = 8
    c: Coincident(g116,g127)
    c: Coincident(g113,g127)
    c: Coincident(g112,g126)
    c: Coincident(g109,g126)
    c: Coincident(g108,g125)
    c: Coincident(g105,g125)
    c: Coincident(g104,g124)
    c: Coincident(g101,g124)
    c: Coincident(g100,g123)
    c: Coincident(g97,g123)
    c: Coincident(g96,g122)
    c: Coincident(g93,g122)
    c: Coincident(g92,g121)
    c: Coincident(g89,g121)
    c: Coincident(g88,g120)
    c: Coincident(g85,g120)
    c: Equal(g91,g87)
    c: Equal(g87,g95)
    c: Equal(g95,g99)
    c: Equal(g99,g103)
    c: Equal(g103,g107)
    c: Equal(g107,g115)
    c: Equal(g115,g111)
    c: Equal(g111,g119)
    c: Coincident(g128,g117)
    c: Coincident(g84,g129)
    c: Coincident(g0,g129)
    c: DistanceY(g87,g87) = 30
    c: Equal(g122,g121)
    c: Equal(g121,g123)
    c: Equal(g123,g124)
    c: Equal(g124,g125)
    c: Equal(g125,g126)
    c: Equal(g126,g127)
    c: Equal(g127,g128)
    c: PointOnObject(g118,g3)
    c: PointOnObject(g114,g3)
    c: PointOnObject(g110,g3)
    c: PointOnObject(g106,g3)
    c: PointOnObject(g102,g3)
    c: PointOnObject(g98,g3)
    c: PointOnObject(g94,g3)
    c: PointOnObject(g90,g3)
    c: PointOnObject(g86,g3)
    c: PointOnObject(g4,g3)
    c: Coincident(g128,g2)
    c: Coincident(g130,g131)
    c: Coincident(g131,g132)
    c: Coincident(g132,g133)
    c: Coincident(g133,g130)
    c: Horizontal(g130)
    c: Horizontal(g132)
    c: Vertical(g131)
    c: Vertical(g133)
    c: Coincident(g134,g135)
    c: Coincident(g135,g136)
    c: Coincident(g136,g137)
    c: Coincident(g137,g134)
    c: Horizontal(g134)
    c: Horizontal(g136)
    c: Vertical(g135)
    c: Vertical(g137)
    c: Coincident(g138,g139)
    c: Coincident(g139,g140)
    c: Coincident(g140,g141)
    c: Coincident(g141,g138)
    c: Horizontal(g138)
    c: Horizontal(g140)
    c: Vertical(g139)
    c: Vertical(g141)
    c: Coincident(g142,g143)
    c: Coincident(g143,g144)
    c: Coincident(g144,g145)
    c: Coincident(g145,g142)
    c: Horizontal(g142)
    c: Horizontal(g144)
    c: Vertical(g143)
    c: Vertical(g145)
    c: Coincident(g146,g147)
    c: Coincident(g147,g148)
    c: Coincident(g148,g149)
    c: Coincident(g149,g146)
    c: Horizontal(g146)
    c: Horizontal(g148)
    c: Vertical(g147)
    c: Vertical(g149)
    c: Coincident(g150,g151)
    c: Coincident(g151,g152)
    c: Coincident(g152,g153)
    c: Coincident(g153,g150)
    c: Horizontal(g150)
    c: Horizontal(g152)
    c: Vertical(g151)
    c: Vertical(g153)
    c: Coincident(g154,g155)
    c: Coincident(g155,g156)
    c: Coincident(g156,g157)
    c: Coincident(g157,g154)
    c: Horizontal(g154)
    c: Horizontal(g156)
    c: Vertical(g155)
    c: Vertical(g157)
    c: Coincident(g158,g159)
    c: Coincident(g159,g160)
    c: Coincident(g160,g161)
    c: Coincident(g161,g158)
    c: Horizontal(g158)
    c: Horizontal(g160)
    c: Vertical(g159)
    c: Vertical(g161)
    c: Coincident(g162,g163)
    c: Coincident(g163,g164)
    c: Coincident(g164,g165)
    c: Coincident(g165,g162)
    c: Horizontal(g162)
    c: Horizontal(g164)
    c: Vertical(g163)
    c: Vertical(g165)
    c: Equal(g164,g158)
    c: Equal(g158,g154)
    c: Equal(g154,g150)
    c: Equal(g150,g146)
    c: Equal(g146,g142)
    c: Equal(g142,g138)
    c: Equal(g138,g134)
    c: Equal(g134,g130)
    c: DistanceX(g162,g162) = 8
    c: Equal(g163,g159)
    c: Equal(g159,g155)
    c: Equal(g155,g151)
    c: Equal(g151,g147)
    c: Equal(g147,g143)
    c: Equal(g143,g139)
    c: Equal(g139,g135)
    c: Equal(g135,g131)
    c: Coincident(g158,g166)
    c: Coincident(g164,g166)
    c: Coincident(g160,g167)
    c: Coincident(g154,g167)
    c: Coincident(g156,g168)
    c: Coincident(g150,g168)
    c: Coincident(g152,g169)
    c: Coincident(g146,g169)
    c: Coincident(g148,g170)
    c: Coincident(g142,g170)
    c: Coincident(g144,g171)
    c: Coincident(g138,g171)
    c: Coincident(g140,g172)
    c: Coincident(g134,g172)
    c: Coincident(g136,g173)
    c: Coincident(g130,g173)
    c: Coincident(g162,g174)
    c: Equal(g174,g166)
    c: Equal(g166,g167)
    c: Equal(g167,g168)
    c: Equal(g168,g169)
    c: Equal(g169,g170)
    c: Equal(g170,g171)
    c: Equal(g171,g172)
    c: Equal(g172,g173)
    c: Vertical(g173)
    c: Vertical(g172)
    c: Vertical(g171)
    c: Vertical(g170)
    c: Vertical(g168)
    c: Vertical(g167)
    c: Vertical(g166)
    c: Vertical(g174)
    c: Vertical(g169)
    c: Coincident(g132,g175)
    c: Equal(g175,g173)
    c: DistanceY(g131,g131) = 30
    c: Coincident(g2,g175)
    c: Horizontal(g2)
    c: Coincident(g174,g0)
    c: Symmetric(g2,g0,g-1)
    c: Symmetric(g0,g0,g-2)
    c: Equal(g129,g120)
    c: Equal(g120,g121)
    c: DistanceY(g2,g4) = 10
    c: Horizontal(g4)
    c: Radius(g176) = 1.55
    c: DistanceY(g48,g176) = 5
    c: DistanceX(g176,g164) = 10
    c: Radius(g177) = 1.55
    c: DistanceX(g86,g177) = 10
    c: DistanceY(g37,g177) = 5
    c: Radius(g178) = 1.55
    c: DistanceX(g118,g178) = 10
    c: DistanceY(g7,g178) = 5
    c: DistanceY(g18,g179) = 5
    c: DistanceX(g179,g132) = 10
    c: Radius(g179) = 1.55
    c: Radius(g180) = 1.55
    c: DistanceX(g102,g180) = 10
    c: DistanceY(g102,g180) = 5
    c: Radius(g181) = 1.55
    c: DistanceX(g181,g148) = 10
    c: DistanceY(g148,g181) = 5
FEATURE [Sketcher::SketchObject] Sketch006  label="front"
  sketch-geometry (172):
    g0: LineSegment StartX=-202.5 StartY=329 StartZ=0 EndX=202.5 EndY=329 EndZ=0
    g1: LineSegment [constr] StartX=202.5 StartY=329 StartZ=0 EndX=202.5 EndY=-329 EndZ=0
    g2: LineSegment StartX=202.5 StartY=-329 StartZ=0 EndX=-202.5 EndY=-329 EndZ=0
    g3: LineSegment [constr] StartX=-202.5 StartY=-329 StartZ=0 EndX=-202.5 EndY=329 EndZ=0
    g4: LineSegment [constr] StartX=-202.5 StartY=-319 StartZ=0 EndX=202.5 EndY=-319 EndZ=0
    g5: LineSegment StartX=-145.5 StartY=-319 StartZ=0 EndX=-115.5 EndY=-319 EndZ=0
    g6: LineSegment StartX=-115.5 StartY=-319 StartZ=0 EndX=-115.5 EndY=-311 EndZ=0
    g7: LineSegment StartX=-115.5 StartY=-311 StartZ=0 EndX=-145.5 EndY=-311 EndZ=0
    g8: LineSegment StartX=-145.5 StartY=-311 StartZ=0 EndX=-145.5 EndY=-319 EndZ=0
    g9: LineSegment StartX=-58.5 StartY=-319 StartZ=0 EndX=-28.5 EndY=-319 EndZ=0
    g10: LineSegment StartX=-28.5 StartY=-319 StartZ=0 EndX=-28.5 EndY=-311 EndZ=0
    g11: LineSegment StartX=-28.5 StartY=-311 StartZ=0 EndX=-58.5 EndY=-311 EndZ=0
    g12: LineSegment StartX=-58.5 StartY=-311 StartZ=0 EndX=-58.5 EndY=-319 EndZ=0
    g13: LineSegment StartX=28.5 StartY=-319 StartZ=0 EndX=58.5 EndY=-319 EndZ=0
    g14: LineSegment StartX=58.5 StartY=-319 StartZ=0 EndX=58.5 EndY=-311 EndZ=0
    g15: LineSegment StartX=58.5 StartY=-311 StartZ=0 EndX=28.5 EndY=-311 EndZ=0
    g16: LineSegment StartX=28.5 StartY=-311 StartZ=0 EndX=28.5 EndY=-319 EndZ=0
    g17: LineSegment StartX=115.5 StartY=-319 StartZ=0 EndX=145.5 EndY=-319 EndZ=0
    g18: LineSegment StartX=145.5 StartY=-319 StartZ=0 EndX=145.5 EndY=-311 EndZ=0
    g19: LineSegment StartX=145.5 StartY=-311 StartZ=0 EndX=115.5 EndY=-311 EndZ=0
    g20: LineSegment StartX=115.5 StartY=-311 StartZ=0 EndX=115.5 EndY=-319 EndZ=0
    g21: LineSegment [constr] StartX=-202.5 StartY=-319 StartZ=0 EndX=-145.5 EndY=-319 EndZ=0
    g22: LineSegment [constr] StartX=-115.5 StartY=-319 StartZ=0 EndX=-58.5 EndY=-319 EndZ=0
    g23: LineSegment [constr] StartX=-28.5 StartY=-319 StartZ=0 EndX=28.5 EndY=-319 EndZ=0
    g24: LineSegment [constr] StartX=58.5 StartY=-319 StartZ=0 EndX=115.5 EndY=-319 EndZ=0
    g25: LineSegment [constr] StartX=145.5 StartY=-319 StartZ=0 EndX=202.5 EndY=-319 EndZ=0
    g26: LineSegment [constr] StartX=-202.5 StartY=241 StartZ=0 EndX=202.5 EndY=241 EndZ=0
    g27: LineSegment StartX=-145.5 StartY=241 StartZ=0 EndX=-115.5 EndY=241 EndZ=0
    g28: LineSegment StartX=-115.5 StartY=241 StartZ=0 EndX=-115.5 EndY=249 EndZ=0
    g29: LineSegment StartX=-115.5 StartY=249 StartZ=0 EndX=-145.5 EndY=249 EndZ=0
    g30: LineSegment StartX=-145.5 StartY=249 StartZ=0 EndX=-145.5 EndY=241 EndZ=0
    g31: LineSegment StartX=-58.5 StartY=241 StartZ=0 EndX=-28.5 EndY=241 EndZ=0
    g32: LineSegment StartX=-28.5 StartY=241 StartZ=0 EndX=-28.5 EndY=249 EndZ=0
    g33: LineSegment StartX=-28.5 StartY=249 StartZ=0 EndX=-58.5 EndY=249 EndZ=0
    g34: LineSegment StartX=-58.5 StartY=249 StartZ=0 EndX=-58.5 EndY=241 EndZ=0
    g35: LineSegment StartX=28.5 StartY=241 StartZ=0 EndX=58.5 EndY=241 EndZ=0
    g36: LineSegment StartX=58.5 StartY=241 StartZ=0 EndX=58.5 EndY=249 EndZ=0
    g37: LineSegment StartX=58.5 StartY=249 StartZ=0 EndX=28.5 EndY=249 EndZ=0
    g38: LineSegment StartX=28.5 StartY=249 StartZ=0 EndX=28.5 EndY=241 EndZ=0
    g39: LineSegment StartX=115.5 StartY=249 StartZ=0 EndX=145.5 EndY=249 EndZ=0
    g40: LineSegment StartX=145.5 StartY=249 StartZ=0 EndX=145.5 EndY=241 EndZ=0
    g41: LineSegment StartX=145.5 StartY=241 StartZ=0 EndX=115.5 EndY=241 EndZ=0
    g42: LineSegment StartX=115.5 StartY=241 StartZ=0 EndX=115.5 EndY=249 EndZ=0
    g43: LineSegment [constr] StartX=-202.5 StartY=241 StartZ=0 EndX=-145.5 EndY=241 EndZ=0
    g44: LineSegment [constr] StartX=-115.5 StartY=241 StartZ=0 EndX=-58.5 EndY=241 EndZ=0
    g45: LineSegment [constr] StartX=-28.5 StartY=241 StartZ=0 EndX=28.5 EndY=241 EndZ=0
    g46: LineSegment [constr] StartX=58.5 StartY=241 StartZ=0 EndX=115.5 EndY=241 EndZ=0
    g47: LineSegment [constr] StartX=145.5 StartY=241 StartZ=0 EndX=202.5 EndY=241 EndZ=0
    g48: LineSegment StartX=-210.5 StartY=290.2 StartZ=0 EndX=-202.5 EndY=290.2 EndZ=0
    g49: LineSegment [constr] StartX=-202.5 StartY=290.2 StartZ=0 EndX=-202.5 EndY=260.2 EndZ=0
    g50: LineSegment StartX=-202.5 StartY=260.2 StartZ=0 EndX=-210.5 EndY=260.2 EndZ=0
    g51: LineSegment StartX=-210.5 StartY=260.2 StartZ=0 EndX=-210.5 EndY=290.2 EndZ=0
    g52: LineSegment StartX=-210.5 StartY=221.4 StartZ=0 EndX=-202.5 EndY=221.4 EndZ=0
    g53: LineSegment [constr] StartX=-202.5 StartY=221.4 StartZ=0 EndX=-202.5 EndY=191.4 EndZ=0
    g54: LineSegment StartX=-202.5 StartY=191.4 StartZ=0 EndX=-210.5 EndY=191.4 EndZ=0
    g55: LineSegment StartX=-210.5 StartY=191.4 StartZ=0 EndX=-210.5 EndY=221.4 EndZ=0
    g56: LineSegment StartX=-210.5 StartY=152.6 StartZ=0 EndX=-202.5 EndY=152.6 EndZ=0
    g57: LineSegment [constr] StartX=-202.5 StartY=152.6 StartZ=0 EndX=-202.5 EndY=122.6 EndZ=0
    g58: LineSegment StartX=-202.5 StartY=122.6 StartZ=0 EndX=-210.5 EndY=122.6 EndZ=0
    g59: LineSegment StartX=-210.5 StartY=122.6 StartZ=0 EndX=-210.5 EndY=152.6 EndZ=0
    g60: LineSegment StartX=-210.5 StartY=83.8 StartZ=0 EndX=-202.5 EndY=83.8 EndZ=0
    g61: LineSegment [constr] StartX=-202.5 StartY=83.8 StartZ=0 EndX=-202.5 EndY=53.8 EndZ=0
    g62: LineSegment StartX=-202.5 StartY=53.8 StartZ=0 EndX=-210.5 EndY=53.8 EndZ=0
    g63: LineSegment StartX=-210.5 StartY=53.8 StartZ=0 EndX=-210.5 EndY=83.8 EndZ=0
    g64: LineSegment StartX=-210.5 StartY=15 StartZ=0 EndX=-202.5 EndY=15 EndZ=0
    g65: LineSegment [constr] StartX=-202.5 StartY=15 StartZ=0 EndX=-202.5 EndY=-15 EndZ=0
    g66: LineSegment StartX=-202.5 StartY=-15 StartZ=0 EndX=-210.5 EndY=-15 EndZ=0
    g67: LineSegment StartX=-210.5 StartY=-15 StartZ=0 EndX=-210.5 EndY=15 EndZ=0
    g68: LineSegment StartX=-210.5 StartY=-53.8 StartZ=0 EndX=-202.5 EndY=-53.8 EndZ=0
    g69: LineSegment [constr] StartX=-202.5 StartY=-53.8 StartZ=0 EndX=-202.5 EndY=-83.8 EndZ=0
    g70: LineSegment StartX=-202.5 StartY=-83.8 StartZ=0 EndX=-210.5 EndY=-83.8 EndZ=0
    g71: LineSegment StartX=-210.5 StartY=-83.8 StartZ=0 EndX=-210.5 EndY=-53.8 EndZ=0
    g72: LineSegment StartX=-210.5 StartY=-122.6 StartZ=0 EndX=-202.5 EndY=-122.6 EndZ=0
    g73: LineSegment [constr] StartX=-202.5 StartY=-122.6 StartZ=0 EndX=-202.5 EndY=-152.6 EndZ=0
    g74: LineSegment StartX=-202.5 StartY=-152.6 StartZ=0 EndX=-210.5 EndY=-152.6 EndZ=0
    g75: LineSegment StartX=-210.5 StartY=-152.6 StartZ=0 EndX=-210.5 EndY=-122.6 EndZ=0
    g76: LineSegment StartX=-210.5 StartY=-191.4 StartZ=0 EndX=-202.5 EndY=-191.4 EndZ=0
    g77: LineSegment [constr] StartX=-202.5 StartY=-191.4 StartZ=0 EndX=-202.5 EndY=-221.4 EndZ=0
    g78: LineSegment StartX=-202.5 StartY=-221.4 StartZ=0 EndX=-210.5 EndY=-221.4 EndZ=0
    g79: LineSegment StartX=-210.5 StartY=-221.4 StartZ=0 EndX=-210.5 EndY=-191.4 EndZ=0
    g80: LineSegment StartX=-210.5 StartY=-260.2 StartZ=0 EndX=-202.5 EndY=-260.2 EndZ=0
    g81: LineSegment [constr] StartX=-202.5 StartY=-260.2 StartZ=0 EndX=-202.5 EndY=-290.2 EndZ=0
    g82: LineSegment StartX=-202.5 StartY=-290.2 StartZ=0 EndX=-210.5 EndY=-290.2 EndZ=0
    g83: LineSegment StartX=-210.5 StartY=-290.2 StartZ=0 EndX=-210.5 EndY=-260.2 EndZ=0
    g84: LineSegment StartX=-202.5 StartY=260.2 StartZ=0 EndX=-202.5 EndY=221.4 EndZ=0
    g85: LineSegment StartX=-202.5 StartY=191.4 StartZ=0 EndX=-202.5 EndY=152.6 EndZ=0
    g86: LineSegment StartX=-202.5 StartY=122.6 StartZ=0 EndX=-202.5 EndY=83.8 EndZ=0
    g87: LineSegment StartX=-202.5 StartY=15 StartZ=0 EndX=-202.5 EndY=53.8 EndZ=0
    g88: LineSegment StartX=-202.5 StartY=-53.8 StartZ=0 EndX=-202.5 EndY=-15 EndZ=0
    g89: LineSegment StartX=-202.5 StartY=-122.6 StartZ=0 EndX=-202.5 EndY=-83.8 EndZ=0
    g90: LineSegment StartX=-202.5 StartY=-191.4 StartZ=0 EndX=-202.5 EndY=-152.6 EndZ=0
    g91: LineSegment StartX=-202.5 StartY=-260.2 StartZ=0 EndX=-202.5 EndY=-221.4 EndZ=0
    g92: LineSegment StartX=-202.5 StartY=-329 StartZ=0 EndX=-202.5 EndY=-290.2 EndZ=0
    g93: LineSegment StartX=-202.5 StartY=329 StartZ=0 EndX=-202.5 EndY=290.2 EndZ=0
    g94: LineSegment StartX=202.5 StartY=-260.2 StartZ=0 EndX=210.5 EndY=-260.2 EndZ=0
    g95: LineSegment StartX=210.5 StartY=-260.2 StartZ=0 EndX=210.5 EndY=-290.2 EndZ=0
    g96: LineSegment StartX=210.5 StartY=-290.2 StartZ=0 EndX=202.5 EndY=-290.2 EndZ=0
    g97: LineSegment [constr] StartX=202.5 StartY=-290.2 StartZ=0 EndX=202.5 EndY=-260.2 EndZ=0
    g98: LineSegment StartX=202.5 StartY=-191.4 StartZ=0 EndX=210.5 EndY=-191.4 EndZ=0
    g99: LineSegment StartX=210.5 StartY=-191.4 StartZ=0 EndX=210.5 EndY=-221.4 EndZ=0
    g100: LineSegment StartX=210.5 StartY=-221.4 StartZ=0 EndX=202.5 EndY=-221.4 EndZ=0
    g101: LineSegment [constr] StartX=202.5 StartY=-221.4 StartZ=0 EndX=202.5 EndY=-191.4 EndZ=0
    g102: LineSegment StartX=202.5 StartY=-122.6 StartZ=0 EndX=210.5 EndY=-122.6 EndZ=0
    g103: LineSegment StartX=210.5 StartY=-122.6 StartZ=0 EndX=210.5 EndY=-152.6 EndZ=0
    g104: LineSegment StartX=210.5 StartY=-152.6 StartZ=0 EndX=202.5 EndY=-152.6 EndZ=0
    g105: LineSegment [constr] StartX=202.5 StartY=-152.6 StartZ=0 EndX=202.5 EndY=-122.6 EndZ=0
    g106: LineSegment StartX=202.5 StartY=-53.8 StartZ=0 EndX=210.5 EndY=-53.8 EndZ=0
    g107: LineSegment StartX=210.5 StartY=-53.8 StartZ=0 EndX=210.5 EndY=-83.8 EndZ=0
    g108: LineSegment StartX=210.5 StartY=-83.8 StartZ=0 EndX=202.5 EndY=-83.8 EndZ=0
    g109: LineSegment [constr] StartX=202.5 StartY=-83.8 StartZ=0 EndX=202.5 EndY=-53.8 EndZ=0
    g110: LineSegment StartX=202.5 StartY=15 StartZ=0 EndX=210.5 EndY=15 EndZ=0
    g111: LineSegment StartX=210.5 StartY=15 StartZ=0 EndX=210.5 EndY=-15 EndZ=0
    g112: LineSegment StartX=210.5 StartY=-15 StartZ=0 EndX=202.5 EndY=-15 EndZ=0
    g113: LineSegment [constr] StartX=202.5 StartY=-15 StartZ=0 EndX=202.5 EndY=15 EndZ=0
    g114: LineSegment StartX=202.5 StartY=83.8 StartZ=0 EndX=210.5 EndY=83.8 EndZ=0
    g115: LineSegment StartX=210.5 StartY=83.8 StartZ=0 EndX=210.5 EndY=53.8 EndZ=0
    g116: LineSegment StartX=210.5 StartY=53.8 StartZ=0 EndX=202.5 EndY=53.8 EndZ=0
    g117: LineSegment [constr] StartX=202.5 StartY=53.8 StartZ=0 EndX=202.5 EndY=83.8 EndZ=0
    g118: LineSegment StartX=202.5 StartY=152.6 StartZ=0 EndX=210.5 EndY=152.6 EndZ=0
    g119: LineSegment StartX=210.5 StartY=152.6 StartZ=0 EndX=210.5 EndY=122.6 EndZ=0
    g120: LineSegment StartX=210.5 StartY=122.6 StartZ=0 EndX=202.5 EndY=122.6 EndZ=0
    g121: LineSegment [constr] StartX=202.5 StartY=122.6 StartZ=0 EndX=202.5 EndY=152.6 EndZ=0
    g122: LineSegment StartX=202.5 StartY=221.4 StartZ=0 EndX=210.5 EndY=221.4 EndZ=0
    g123: LineSegment StartX=210.5 StartY=221.4 StartZ=0 EndX=210.5 EndY=191.4 EndZ=0
    g124: LineSegment StartX=210.5 StartY=191.4 StartZ=0 EndX=202.5 EndY=191.4 EndZ=0
    g125: LineSegment [constr] StartX=202.5 StartY=191.4 StartZ=0 EndX=202.5 EndY=221.4 EndZ=0
    g126: LineSegment StartX=202.5 StartY=290.2 StartZ=0 EndX=210.5 EndY=290.2 EndZ=0
    g127: LineSegment StartX=210.5 StartY=290.2 StartZ=0 EndX=210.5 EndY=260.2 EndZ=0
    g128: LineSegment StartX=210.5 StartY=260.2 StartZ=0 EndX=202.5 EndY=260.2 EndZ=0
    g129: LineSegment [constr] StartX=202.5 StartY=260.2 StartZ=0 EndX=202.5 EndY=290.2 EndZ=0
    g130: LineSegment StartX=202.5 StartY=260.2 StartZ=0 EndX=202.5 EndY=221.4 EndZ=0
    g131: LineSegment StartX=202.5 StartY=191.4 StartZ=0 EndX=202.5 EndY=152.6 EndZ=0
    g132: LineSegment StartX=202.5 StartY=83.8 StartZ=0 EndX=202.5 EndY=122.6 EndZ=0
    g133: LineSegment StartX=202.5 StartY=15 StartZ=0 EndX=202.5 EndY=53.8 EndZ=0
    g134: LineSegment StartX=202.5 StartY=-53.8 StartZ=0 EndX=202.5 EndY=-15 EndZ=0
    g135: LineSegment StartX=202.5 StartY=-122.6 StartZ=0 EndX=202.5 EndY=-83.8 EndZ=0
    g136: LineSegment StartX=202.5 StartY=-191.4 StartZ=0 EndX=202.5 EndY=-152.6 EndZ=0
    g137: LineSegment StartX=202.5 StartY=-260.2 StartZ=0 EndX=202.5 EndY=-221.4 EndZ=0
    g138: LineSegment StartX=202.5 StartY=290.2 StartZ=0 EndX=202.5 EndY=329 EndZ=0
    g139: LineSegment StartX=202.5 StartY=-290.2 StartZ=0 EndX=202.5 EndY=-329 EndZ=0
    g140: LineSegment [constr] StartX=-160 StartY=169 StartZ=0 EndX=160 EndY=169 EndZ=0
    g141: LineSegment StartX=160 StartY=169 StartZ=0 EndX=160 EndY=-249 EndZ=0
    g142: LineSegment [constr] StartX=160 StartY=-249 StartZ=0 EndX=-160 EndY=-249 EndZ=0
    g143: LineSegment StartX=-160 StartY=-249 StartZ=0 EndX=-160 EndY=169 EndZ=0
    g144: ArcOfCircle CenterX=-2.017e-13 CenterY=534.837 CenterZ=0 NormalX=0 NormalY=0 NormalZ=1 AngleXU=0 Radius=800 StartAngle=4.51103 EndAngle=4.91375
    g145: ArcOfCircle CenterX=5.13e-14 CenterY=-614.837 CenterZ=0 NormalX=0 NormalY=0 NormalZ=1 AngleXU=0 Radius=800 StartAngle=1.36944 EndAngle=1.77215
    g146: LineSegment [constr] StartX=-43 StartY=312.5 StartZ=0 EndX=43 EndY=312.5 EndZ=0
    g147: LineSegment [constr] StartX=43 StartY=312.5 StartZ=0 EndX=43 EndY=265.5 EndZ=0
    g148: LineSegment [constr] StartX=43 StartY=265.5 StartZ=0 EndX=-43 EndY=265.5 EndZ=0
    g149: LineSegment [constr] StartX=-43 StartY=265.5 StartZ=0 EndX=-43 EndY=312.5 EndZ=0
    g150: LineSegment [constr] StartX=-43 StartY=312.5 StartZ=0 EndX=-43 EndY=329 EndZ=0
    g151: LineSegment [constr] StartX=-43 StartY=249 StartZ=0 EndX=-43 EndY=265.5 EndZ=0
    g152: Circle [constr] CenterX=-43 CenterY=312.5 CenterZ=0 NormalX=0 NormalY=0 NormalZ=1 AngleXU=0 Radius=1.55
    g153: Circle [constr] CenterX=-43 CenterY=265.5 CenterZ=0 NormalX=0 NormalY=0 NormalZ=1 AngleXU=0 Radius=1.55
    g154: Circle [constr] CenterX=43 CenterY=265.5 CenterZ=0 NormalX=0 NormalY=0 NormalZ=1 AngleXU=0 Radius=1.55
    g155: Circle [constr] CenterX=43 CenterY=312.5 CenterZ=0 NormalX=0 NormalY=0 NormalZ=1 AngleXU=0 Radius=1.55
    g156: LineSegment StartX=-31 StartY=309.5 StartZ=0 EndX=21 EndY=309.5 EndZ=0
    g157: LineSegment StartX=21 StartY=309.5 StartZ=0 EndX=21 EndY=268.5 EndZ=0
    g158: LineSegment StartX=21 StartY=268.5 StartZ=0 EndX=-31 EndY=268.5 EndZ=0
    g159: LineSegment StartX=-31 StartY=268.5 StartZ=0 EndX=-31 EndY=309.5 EndZ=0
    g160: Circle CenterX=33 CenterY=272.5 CenterZ=0 NormalX=0 NormalY=0 NormalZ=1 AngleXU=0 Radius=2.5
    g161: Circle CenterX=33 CenterY=288.5 CenterZ=0 NormalX=0 NormalY=0 NormalZ=1 AngleXU=0 Radius=7.5
    g162: LineSegment StartX=-54 StartY=306.5 StartZ=0 EndX=-46 EndY=306.5 EndZ=0
    g163: LineSegment StartX=-46 StartY=306.5 StartZ=0 EndX=-46 EndY=270.5 EndZ=0
    g164: LineSegment StartX=-46 StartY=270.5 StartZ=0 EndX=-54 EndY=270.5 EndZ=0
    g165: LineSegment StartX=-54 StartY=270.5 StartZ=0 EndX=-54 EndY=306.5 EndZ=0
    g166: Circle CenterX=-192.5 CenterY=254 CenterZ=0 NormalX=0 NormalY=0 NormalZ=1 AngleXU=0 Radius=1.55
    g167: Circle CenterX=192.5 CenterY=254 CenterZ=0 NormalX=0 NormalY=0 NormalZ=1 AngleXU=0 Radius=1.55
    g168: Circle CenterX=-192.5 CenterY=-10 CenterZ=0 NormalX=0 NormalY=0 NormalZ=1 AngleXU=0 Radius=1.55
    g169: Circle CenterX=192.5 CenterY=-10 CenterZ=0 NormalX=0 NormalY=0 NormalZ=1 AngleXU=0 Radius=1.55
    g170: Circle CenterX=-192.5 CenterY=-306 CenterZ=0 NormalX=0 NormalY=0 NormalZ=1 AngleXU=0 Radius=1.55
    g171: Circle CenterX=192.5 CenterY=-306 CenterZ=0 NormalX=0 NormalY=0 NormalZ=1 AngleXU=0 Radius=1.55
  constraints (480):
    c: Coincident(g0,g1)
    c: Coincident(g1,g2)
    c: Coincident(g2,g3)
    c: Coincident(g3,g0)
    c: Vertical(g1)
    c: DistanceX(g2,g2) = 405
    c: PointOnObject(g4,g1)
    c: Coincident(g5,g6)
    c: Coincident(g6,g7)
    c: Coincident(g7,g8)
    c: Coincident(g8,g5)
    c: Horizontal(g5)
    c: Horizontal(g7)
    c: Vertical(g6)
    c: Vertical(g8)
    c: Coincident(g9,g10)
    c: Coincident(g10,g11)
    c: Coincident(g11,g12)
    c: Coincident(g12,g9)
    c: Horizontal(g9)
    c: Horizontal(g11)
    c: Vertical(g10)
    c: Vertical(g12)
    c: Coincident(g13,g14)
    c: Coincident(g14,g15)
    c: Coincident(g15,g16)
    c: Coincident(g16,g13)
    c: Horizontal(g13)
    c: Horizontal(g15)
    c: Vertical(g14)
    c: Vertical(g16)
    c: Coincident(g17,g18)
    c: Coincident(g18,g19)
    c: Coincident(g19,g20)
    c: Coincident(g20,g17)
    c: Horizontal(g17)
    c: Horizontal(g19)
    c: Vertical(g18)
    c: Vertical(g20)
    c: Equal(g17,g13)
    c: Equal(g13,g9)
    c: Equal(g9,g5)
    c: DistanceX(g7,g7) = 30
    c: PointOnObject(g5,g4)
    c: PointOnObject(g9,g4)
    c: PointOnObject(g13,g4)
    c: PointOnObject(g17,g4)
    c: Equal(g20,g14)
    c: Equal(g14,g12)
    c: Equal(g12,g6)
    c: DistanceY(g8,g8) = 8
    c: Equal(g25,g24)
    c: Equal(g24,g23)
    c: Equal(g23,g22)
    c: Equal(g22,g21)
    c: Coincident(g4,g25)
    c: Coincident(g17,g25)
    c: Coincident(g17,g24)
    c: Coincident(g13,g24)
    c: Coincident(g13,g23)
    c: Coincident(g9,g23)
    c: Coincident(g22,g9)
    c: Coincident(g5,g22)
    c: Coincident(g5,g21)
    c: Coincident(g4,g21)
    c: DistanceY(g3,g3) = 658
    c: Horizontal(g26)
    c: Coincident(g27,g28)
    c: Coincident(g28,g29)
    c: Coincident(g29,g30)
    c: Coincident(g30,g27)
    c: Horizontal(g27)
    c: Horizontal(g29)
    c: Vertical(g28)
    c: Vertical(g30)
    c: Coincident(g31,g32)
    c: Coincident(g32,g33)
    c: Coincident(g33,g34)
    c: Coincident(g34,g31)
    c: Horizontal(g31)
    c: Horizontal(g33)
    c: Vertical(g32)
    c: Vertical(g34)
    c: Coincident(g35,g36)
    c: Coincident(g36,g37)
    c: Coincident(g37,g38)
    c: Coincident(g38,g35)
    c: Horizontal(g35)
    c: Horizontal(g37)
    c: Vertical(g36)
    c: Vertical(g38)
    c: Coincident(g40,g41)
    c: Coincident(g41,g42)
    c: Horizontal(g39)
    c: Horizontal(g41)
    c: Vertical(g40)
    c: Vertical(g42)
    c: Equal(g39,g35)
    c: Equal(g35,g31)
    c: Equal(g31,g27)
    c: Equal(g7,g29) = 30
    c: PointOnObject(g27,g26)
    c: PointOnObject(g31,g26)
    c: PointOnObject(g35,g26)
    c: Equal(g42,g36)
    c: Equal(g36,g34)
    c: Equal(g34,g28)
    c: Equal(g8,g30) = 8
    c: Equal(g47,g46)
    c: Equal(g46,g45)
    c: Equal(g45,g44)
    c: Equal(g44,g43)
    c: Coincident(g26,g47)
    c: Coincident(g35,g46)
    c: Coincident(g35,g45)
    c: Coincident(g31,g45)
    c: Coincident(g44,g31)
    c: Coincident(g27,g44)
    c: Coincident(g27,g43)
    c: Coincident(g26,g43)
    c: PointOnObject(g26,g3)
    c: PointOnObject(g26,g1)
    c: DistanceY(g26,g0) = 88
    c: Coincident(g48,g49)
    c: Coincident(g49,g50)
    c: Coincident(g50,g51)
    c: Coincident(g51,g48)
    c: Horizontal(g48)
    c: Horizontal(g50)
    c: Vertical(g49)
    c: Vertical(g51)
    c: Coincident(g52,g53)
    c: Coincident(g53,g54)
    c: Coincident(g54,g55)
    c: Coincident(g55,g52)
    c: Horizontal(g52)
    c: Horizontal(g54)
    c: Vertical(g53)
    c: Vertical(g55)
    c: Coincident(g56,g57)
    c: Coincident(g57,g58)
    c: Coincident(g58,g59)
    c: Coincident(g59,g56)
    c: Horizontal(g56)
    c: Horizontal(g58)
    c: Vertical(g57)
    c: Vertical(g59)
    c: Coincident(g60,g61)
    c: Coincident(g61,g62)
    c: Coincident(g62,g63)
    c: Coincident(g63,g60)
    c: Horizontal(g60)
    c: Horizontal(g62)
    c: Vertical(g61)
    c: Vertical(g63)
    c: Coincident(g64,g65)
    c: Coincident(g65,g66)
    c: Coincident(g66,g67)
    c: Coincident(g67,g64)
    c: Horizontal(g64)
    c: Horizontal(g66)
    c: Vertical(g65)
    c: Vertical(g67)
    c: Coincident(g68,g69)
    c: Coincident(g69,g70)
    c: Coincident(g70,g71)
    c: Coincident(g71,g68)
    c: Horizontal(g68)
    c: Horizontal(g70)
    c: Vertical(g69)
    c: Vertical(g71)
    c: Coincident(g72,g73)
    c: Coincident(g73,g74)
    c: Coincident(g74,g75)
    c: Coincident(g75,g72)
    c: Horizontal(g72)
    c: Horizontal(g74)
    c: Vertical(g73)
    c: Vertical(g75)
    c: Coincident(g76,g77)
    c: Coincident(g77,g78)
    c: Coincident(g78,g79)
    c: Coincident(g79,g76)
    c: Horizontal(g76)
    c: Horizontal(g78)
    c: Vertical(g77)
    c: Vertical(g79)
    c: Coincident(g80,g81)
    c: Coincident(g81,g82)
    c: Coincident(g82,g83)
    c: Coincident(g83,g80)
    c: Horizontal(g80)
    c: Horizontal(g82)
    c: Vertical(g81)
    c: Vertical(g83)
    c: Equal(g82,g78)
    c: Equal(g78,g74)
    c: Equal(g74,g70)
    c: Equal(g70,g66)
    c: Equal(g66,g62)
    c: Equal(g62,g58)
    c: Equal(g58,g54)
    c: Equal(g54,g50)
    c: DistanceX(g48,g48) = 8
    c: Coincident(g80,g91)
    c: Coincident(g77,g91)
    c: Coincident(g76,g90)
    c: Coincident(g73,g90)
    c: Coincident(g72,g89)
    c: Coincident(g69,g89)
    c: Coincident(g68,g88)
    c: Coincident(g65,g88)
    c: Coincident(g64,g87)
    c: Coincident(g61,g87)
    c: Coincident(g60,g86)
    c: Coincident(g57,g86)
    c: Coincident(g56,g85)
    c: Coincident(g53,g85)
    c: Coincident(g52,g84)
    c: Coincident(g49,g84)
    c: Equal(g55,g51)
    c: Equal(g51,g59)
    c: Equal(g59,g63)
    c: Equal(g63,g67)
    c: Equal(g67,g71)
    c: Equal(g71,g79)
    c: Equal(g79,g75)
    c: Equal(g75,g83)
    c: Coincident(g92,g81)
    c: Coincident(g48,g93)
    c: Coincident(g0,g93)
    c: DistanceY(g51,g51) = 30
    c: Equal(g86,g85)
    c: Equal(g85,g87)
    c: Equal(g87,g88)
    c: Equal(g88,g89)
    c: Equal(g89,g90)
    c: Equal(g90,g91)
    c: Equal(g91,g92)
    c: PointOnObject(g82,g3)
    c: PointOnObject(g78,g3)
    c: PointOnObject(g74,g3)
    c: PointOnObject(g70,g3)
    c: PointOnObject(g66,g3)
    c: PointOnObject(g62,g3)
    c: PointOnObject(g58,g3)
    c: PointOnObject(g54,g3)
    c: PointOnObject(g50,g3)
    c: PointOnObject(g4,g3)
    c: Coincident(g92,g2)
    c: Coincident(g94,g95)
    c: Coincident(g95,g96)
    c: Coincident(g96,g97)
    c: Coincident(g97,g94)
    c: Horizontal(g94)
    c: Horizontal(g96)
    c: Vertical(g95)
    c: Vertical(g97)
    c: Coincident(g98,g99)
    c: Coincident(g99,g100)
    c: Coincident(g100,g101)
    c: Coincident(g101,g98)
    c: Horizontal(g98)
    c: Horizontal(g100)
    c: Vertical(g99)
    c: Vertical(g101)
    c: Coincident(g102,g103)
    c: Coincident(g103,g104)
    c: Coincident(g104,g105)
    c: Coincident(g105,g102)
    c: Horizontal(g102)
    c: Horizontal(g104)
    c: Vertical(g103)
    c: Vertical(g105)
    c: Coincident(g106,g107)
    c: Coincident(g107,g108)
    c: Coincident(g108,g109)
    c: Coincident(g109,g106)
    c: Horizontal(g106)
    c: Horizontal(g108)
    c: Vertical(g107)
    c: Vertical(g109)
    c: Coincident(g110,g111)
    c: Coincident(g111,g112)
    c: Coincident(g112,g113)
    c: Coincident(g113,g110)
    c: Horizontal(g110)
    c: Horizontal(g112)
    c: Vertical(g111)
    c: Vertical(g113)
    c: Coincident(g114,g115)
    c: Coincident(g115,g116)
    c: Coincident(g116,g117)
    c: Coincident(g117,g114)
    c: Horizontal(g114)
    c: Horizontal(g116)
    c: Vertical(g115)
    c: Vertical(g117)
    c: Coincident(g118,g119)
    c: Coincident(g119,g120)
    c: Coincident(g120,g121)
    c: Coincident(g121,g118)
    c: Horizontal(g118)
    c: Horizontal(g120)
    c: Vertical(g119)
    c: Vertical(g121)
    c: Coincident(g122,g123)
    c: Coincident(g123,g124)
    c: Coincident(g124,g125)
    c: Coincident(g125,g122)
    c: Horizontal(g122)
    c: Horizontal(g124)
    c: Vertical(g123)
    c: Vertical(g125)
    c: Coincident(g126,g127)
    c: Coincident(g127,g128)
    c: Coincident(g128,g129)
    c: Coincident(g129,g126)
    c: Horizontal(g126)
    c: Horizontal(g128)
    c: Vertical(g127)
    c: Vertical(g129)
    c: Equal(g128,g122)
    c: Equal(g122,g118)
    c: Equal(g118,g114)
    c: Equal(g114,g110)
    c: Equal(g110,g106)
    c: Equal(g106,g102)
    c: Equal(g102,g98)
    c: Equal(g98,g94)
    c: DistanceX(g126,g126) = 8
    c: Equal(g127,g123)
    c: Equal(g123,g119)
    c: Equal(g119,g115)
    c: Equal(g115,g111)
    c: Equal(g111,g107)
    c: Equal(g107,g103)
    c: Equal(g103,g99)
    c: Equal(g99,g95)
    c: Coincident(g122,g130)
    c: Coincident(g128,g130)
    c: Coincident(g124,g131)
    c: Coincident(g118,g131)
    c: Coincident(g120,g132)
    c: Coincident(g114,g132)
    c: Coincident(g116,g133)
    c: Coincident(g110,g133)
    c: Coincident(g112,g134)
    c: Coincident(g106,g134)
    c: Coincident(g108,g135)
    c: Coincident(g102,g135)
    c: Coincident(g104,g136)
    c: Coincident(g98,g136)
    c: Coincident(g100,g137)
    c: Coincident(g94,g137)
    c: Coincident(g126,g138)
    c: Equal(g138,g130)
    c: Equal(g130,g131)
    c: Equal(g131,g132)
    c: Equal(g132,g133)
    c: Equal(g133,g134)
    c: Equal(g134,g135)
    c: Equal(g135,g136)
    c: Equal(g136,g137)
    c: Vertical(g137)
    c: Vertical(g136)
    c: Vertical(g135)
    c: Vertical(g134)
    c: Vertical(g132)
    c: Vertical(g131)
    c: Vertical(g130)
    c: Vertical(g138)
    c: Vertical(g133)
    c: Coincident(g96,g139)
    c: Equal(g139,g137)
    c: DistanceY(g95,g95) = 30
    c: Coincident(g2,g139)
    c: Horizontal(g2)
    c: Coincident(g138,g0)
    c: Symmetric(g2,g0,g-1)
    c: Symmetric(g0,g0,g-2)
    c: Equal(g93,g84)
    c: Equal(g84,g85)
    c: DistanceY(g2,g4) = 10
    c: Horizontal(g4)
    c: Coincident(g140,g141)
    c: Coincident(g141,g142)
    c: Coincident(g142,g143)
    c: Coincident(g143,g140)
    c: Horizontal(g140)
    c: Vertical(g143)
    c: Symmetric(g141,g142,g-2)
    c: DistanceY(g2,g141) = 80
    c: DistanceX(g142,g142) = 320
    c: Vertical(g141)
    c: DistanceY(g140,g39) = 80
    c: Coincident(g142,g144)
    c: Coincident(g141,g144)
    c: Coincident(g140,g145)
    c: Coincident(g140,g145)
    c: Radius(g144) = 800
    c: Equal(g144,g145)
    c: Coincident(g146,g147)
    c: Coincident(g147,g148)
    c: Coincident(g148,g149)
    c: Coincident(g149,g146)
    c: Horizontal(g148)
    c: Vertical(g147)
    c: Vertical(g149)
    c: Symmetric(g146,g146,g-2)
    c: DistanceX(g146,g146) = 86
    c: DistanceY(g147,g147) = 47
    c: Coincident(g148,g151)
    c: PointOnObject(g151,g33)
    c: PointOnObject(g150,g0)
    c: Vertical(g150)
    c: Vertical(g151)
    c: Coincident(g150,g146)
    c: Equal(g150,g151)
    c: Coincident(g146,g155)
    c: Coincident(g147,g154)
    c: Coincident(g148,g153)
    c: Coincident(g146,g152)
    c: Radius(g152) = 1.55
    c: Equal(g152,g155)
    c: Equal(g152,g154)
    c: Equal(g152,g153)
    c: Coincident(g156,g157)
    c: Coincident(g157,g158)
    c: Coincident(g158,g159)
    c: Coincident(g159,g156)
    c: Horizontal(g156)
    c: Horizontal(g158)
    c: Vertical(g157)
    c: Vertical(g159)
    c: DistanceX(g152,g156) = 12
    c: DistanceX(g156,g155) = 22
    c: DistanceY(g156,g152) = 3
    c: DistanceY(g153,g158) = 3
    c: DistanceY(g154,g160) = 7
    c: DistanceX(g160,g154) = 10
    c: Radius(g160) = 2.5
    c: DistanceX(g161,g154) = 10
    c: DistanceY(g160,g161) = 16
    c: Radius(g161) = 7.5
    c: Coincident(g162,g163)
    c: Coincident(g163,g164)
    c: Coincident(g164,g165)
    c: Coincident(g165,g162)
    c: Horizontal(g162)
    c: Horizontal(g164)
    c: Vertical(g163)
    c: Vertical(g165)
    c: DistanceX(g162,g162) = 8
    c: DistanceY(g165,g165) = 36
    c: DistanceX(g163,g153) = 3
    c: DistanceY(g162,g152) = 6
    c: Coincident(g41,g46)
    c: Coincident(g40,g47)
    c: Coincident(g39,g42)
    c: PointOnObject(g41,g26)
    c: Coincident(g39,g40)
    c: Radius(g166) = 1.55
    c: DistanceX(g50,g166) = 10
    c: DistanceY(g29,g166) = 5
    c: Radius(g167) = 1.55
    c: DistanceX(g167,g128) = 10
    c: DistanceY(g39,g167) = 5
    c: DistanceX(g66,g168) = 10
    c: DistanceY(g66,g168) = 5
    c: Radius(g168) = 1.55
    c: DistanceX(g169,g112) = 10
    c: DistanceY(g112,g169) = 5
    c: Radius(g169) = 1.55
    c: DistanceY(g18,g171) = 5
    c: DistanceX(g171,g96) = 10
    c: Radius(g171) = 1.55
    c: DistanceX(g82,g170) = 10
    c: DistanceY(g7,g170) = 5
    c: Radius(g170) = 1.55
